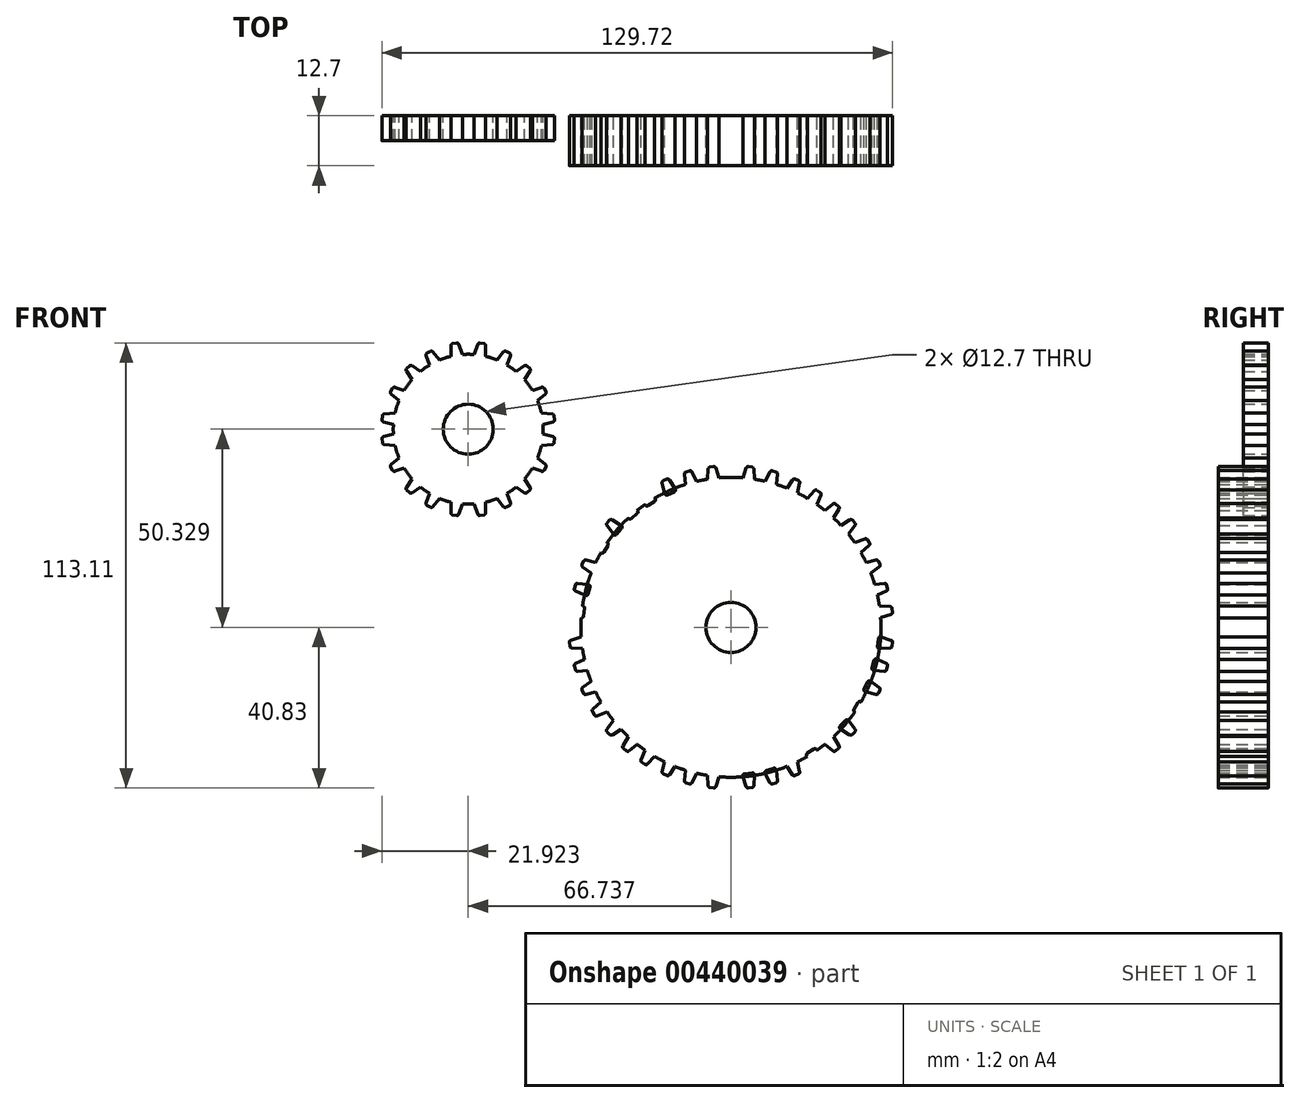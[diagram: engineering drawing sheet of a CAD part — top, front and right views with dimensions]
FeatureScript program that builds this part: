
annotation { "Feature Type Name" : "Feature", "Feature Type Description" : "" }
export const myFeature = defineFeature(function(context is Context, id is Id, definition is map)
    precondition{}
    {
        {
            var Q0;
            Q0=qCreatedBy(makeId("Front.planeOp"),FACE);
            var sketch = newSketch(context, id + "F0", { "sketchPlane" : qUnion([Q0])});
            skCircle(sketch, "E0", {"center": v(0, 0) * mm, "radius": 38.1 * mm});
            skCircle(sketch, "E1", {"center": v(0, 0) * mm, "radius": 6.35 * mm});
            skLineSegment(sketch, "E2", {"start": v(-38.1, 0) * mm, "end": v(38.1, 0) * mm, "construction": true});
            skLineSegment(sketch, "E3", {"start": v(0, 38.1) * mm, "end": v(0, -38.1) * mm, "construction": true});
            skLineSegment(sketch, "E4", {"start": v(35.83, 10.3) * mm, "end": v(36.32, 8.42) * mm});
            skLineSegment(sketch, "E5", {"start": v(39.02, 11.15) * mm, "end": v(36.28, 10.93) * mm});
            skLineSegment(sketch, "E6", {"start": v(37.02, 8.09) * mm, "end": v(39.52, 9.23) * mm});
            skLineSegment(sketch, "E7", {"start": v(39.55, 10.77) * mm, "end": v(39.8, 9.82) * mm});
            skPoint(sketch, "E8.visualSharp", {"position": v(39.44, 11.18) * mm});
            skArc(sketch, "E8.filletArc", {"start": v(39.55, 10.77) * mm, "mid": v(39.35, 11.06) * mm, "end": v(39.02, 11.15) * mm});
            skPoint(sketch, "E9.visualSharp", {"position": v(35.68, 10.88) * mm});
            skArc(sketch, "E9.filletArc", {"start": v(36.28, 10.93) * mm, "mid": v(35.91, 10.72) * mm, "end": v(35.83, 10.3) * mm});
            skPoint(sketch, "E10.visualSharp", {"position": v(36.47, 7.84) * mm});
            skArc(sketch, "E10.filletArc", {"start": v(36.32, 8.42) * mm, "mid": v(36.6, 8.1) * mm, "end": v(37.02, 8.09) * mm});
            skPoint(sketch, "E11.visualSharp", {"position": v(39.9, 9.4) * mm});
            skArc(sketch, "E11.filletArc", {"start": v(39.52, 9.23) * mm, "mid": v(39.76, 9.47) * mm, "end": v(39.8, 9.82) * mm});
            skLineSegment(sketch, "E12", {"start": v(37.18, 4.8) * mm, "end": v(37.43, 2.88) * mm});
            skLineSegment(sketch, "E13", {"start": v(40.44, 5.27) * mm, "end": v(37.7, 5.38) * mm});
            skLineSegment(sketch, "E14", {"start": v(38.1, 2.46) * mm, "end": v(40.7, 3.3) * mm});
            skLineSegment(sketch, "E15", {"start": v(40.92, 4.83) * mm, "end": v(41.05, 3.85) * mm});
            skPoint(sketch, "E16.visualSharp", {"position": v(40.87, 5.25) * mm});
            skArc(sketch, "E16.filletArc", {"start": v(40.92, 4.83) * mm, "mid": v(40.76, 5.13) * mm, "end": v(40.44, 5.27) * mm});
            skPoint(sketch, "E17.visualSharp", {"position": v(37.1, 5.4) * mm});
            skArc(sketch, "E17.filletArc", {"start": v(37.7, 5.38) * mm, "mid": v(37.3, 5.21) * mm, "end": v(37.18, 4.8) * mm});
            skPoint(sketch, "E18.visualSharp", {"position": v(37.52, 2.28) * mm});
            skArc(sketch, "E18.filletArc", {"start": v(37.43, 2.88) * mm, "mid": v(37.67, 2.52) * mm, "end": v(38.1, 2.46) * mm});
            skPoint(sketch, "E19.visualSharp", {"position": v(41.11, 3.43) * mm});
            skArc(sketch, "E19.filletArc", {"start": v(40.7, 3.3) * mm, "mid": v(40.98, 3.5) * mm, "end": v(41.05, 3.85) * mm});
            skLineSegment(sketch, "E20.0", {"start": v(41.11, 3.43) * mm, "end": v(40.87, 5.25) * mm, "construction": true});
            skLineSegment(sketch, "E21.0", {"start": v(39.9, 9.4) * mm, "end": v(39.44, 11.18) * mm, "construction": true});
            skLineSegment(sketch, "E22", {"start": v(33.84, 15.67) * mm, "end": v(34.66, 13.92) * mm});
            skLineSegment(sketch, "E23", {"start": v(36.81, 17.09) * mm, "end": v(34.17, 16.38) * mm});
            skLineSegment(sketch, "E24", {"start": v(35.4, 13.71) * mm, "end": v(37.65, 15.29) * mm});
            skLineSegment(sketch, "E25", {"start": v(37.4, 16.81) * mm, "end": v(37.82, 15.92) * mm});
            skPoint(sketch, "E26.visualSharp", {"position": v(37.23, 17.2) * mm});
            skArc(sketch, "E26.filletArc", {"start": v(37.4, 16.81) * mm, "mid": v(37.16, 17.06) * mm, "end": v(36.81, 17.09) * mm});
            skPoint(sketch, "E27.visualSharp", {"position": v(33.58, 16.22) * mm});
            skArc(sketch, "E27.filletArc", {"start": v(34.17, 16.38) * mm, "mid": v(33.84, 16.1) * mm, "end": v(33.84, 15.67) * mm});
            skPoint(sketch, "E28.visualSharp", {"position": v(34.91, 13.37) * mm});
            skArc(sketch, "E28.filletArc", {"start": v(34.66, 13.92) * mm, "mid": v(34.99, 13.64) * mm, "end": v(35.4, 13.71) * mm});
            skPoint(sketch, "E29.visualSharp", {"position": v(38, 15.53) * mm});
            skArc(sketch, "E29.filletArc", {"start": v(37.65, 15.29) * mm, "mid": v(37.85, 15.57) * mm, "end": v(37.82, 15.92) * mm});
            skLineSegment(sketch, "E30.0", {"start": v(38, 15.53) * mm, "end": v(37.23, 17.2) * mm, "construction": true});
            skLineSegment(sketch, "E31", {"start": v(31.25, 20.8) * mm, "end": v(32.23, 19.13) * mm});
            skLineSegment(sketch, "E32", {"start": v(34.08, 22.48) * mm, "end": v(31.51, 21.53) * mm});
            skLineSegment(sketch, "E33", {"start": v(33, 19) * mm, "end": v(35.09, 20.77) * mm});
            skLineSegment(sketch, "E34", {"start": v(34.7, 22.26) * mm, "end": v(35.2, 21.41) * mm});
            skPoint(sketch, "E35.visualSharp", {"position": v(34.48, 22.63) * mm});
            skArc(sketch, "E35.filletArc", {"start": v(34.7, 22.26) * mm, "mid": v(34.43, 22.49) * mm, "end": v(34.08, 22.48) * mm});
            skPoint(sketch, "E36.visualSharp", {"position": v(30.94, 21.32) * mm});
            skArc(sketch, "E36.filletArc", {"start": v(31.51, 21.53) * mm, "mid": v(31.2, 21.23) * mm, "end": v(31.25, 20.8) * mm});
            skPoint(sketch, "E37.visualSharp", {"position": v(32.53, 18.6) * mm});
            skArc(sketch, "E37.filletArc", {"start": v(32.23, 19.13) * mm, "mid": v(32.58, 18.88) * mm, "end": v(33, 19) * mm});
            skPoint(sketch, "E38.visualSharp", {"position": v(35.41, 21.04) * mm});
            skArc(sketch, "E38.filletArc", {"start": v(35.09, 20.77) * mm, "mid": v(35.26, 21.07) * mm, "end": v(35.2, 21.41) * mm});
            skLineSegment(sketch, "E39.0", {"start": v(35.41, 21.04) * mm, "end": v(34.48, 22.63) * mm, "construction": true});
            skLineSegment(sketch, "E40", {"start": v(27.75, 25.07) * mm, "end": v(29.06, 23.64) * mm});
            skLineSegment(sketch, "E41", {"start": v(30.16, 27.32) * mm, "end": v(27.85, 25.84) * mm});
            skLineSegment(sketch, "E42", {"start": v(29.84, 23.68) * mm, "end": v(31.5, 25.86) * mm});
            skLineSegment(sketch, "E43", {"start": v(30.8, 27.24) * mm, "end": v(31.47, 26.51) * mm});
            skPoint(sketch, "E44.visualSharp", {"position": v(30.52, 27.55) * mm});
            skArc(sketch, "E44.filletArc", {"start": v(30.8, 27.24) * mm, "mid": v(30.5, 27.4) * mm, "end": v(30.16, 27.32) * mm});
            skPoint(sketch, "E45.visualSharp", {"position": v(27.34, 25.51) * mm});
            skArc(sketch, "E45.filletArc", {"start": v(27.85, 25.84) * mm, "mid": v(27.62, 25.48) * mm, "end": v(27.75, 25.07) * mm});
            skPoint(sketch, "E46.visualSharp", {"position": v(29.47, 23.2) * mm});
            skArc(sketch, "E46.filletArc", {"start": v(29.06, 23.64) * mm, "mid": v(29.46, 23.48) * mm, "end": v(29.84, 23.68) * mm});
            skPoint(sketch, "E47.visualSharp", {"position": v(31.76, 26.2) * mm});
            skArc(sketch, "E47.filletArc", {"start": v(31.5, 25.86) * mm, "mid": v(31.6, 26.19) * mm, "end": v(31.47, 26.51) * mm});
            skLineSegment(sketch, "E48.0", {"start": v(31.76, 26.2) * mm, "end": v(30.52, 27.55) * mm, "construction": true});
            skLineSegment(sketch, "E49", {"start": v(23.82, 28.87) * mm, "end": v(25.3, 27.61) * mm});
            skLineSegment(sketch, "E50", {"start": v(25.95, 31.4) * mm, "end": v(23.83, 29.65) * mm});
            skLineSegment(sketch, "E51", {"start": v(26.07, 27.74) * mm, "end": v(27.46, 30.1) * mm});
            skLineSegment(sketch, "E52", {"start": v(26.6, 31.39) * mm, "end": v(27.35, 30.75) * mm});
            skPoint(sketch, "E53.visualSharp", {"position": v(26.28, 31.66) * mm});
            skArc(sketch, "E53.filletArc", {"start": v(26.6, 31.39) * mm, "mid": v(26.27, 31.5) * mm, "end": v(25.95, 31.4) * mm});
            skPoint(sketch, "E54.visualSharp", {"position": v(23.36, 29.26) * mm});
            skArc(sketch, "E54.filletArc", {"start": v(23.83, 29.65) * mm, "mid": v(23.65, 29.26) * mm, "end": v(23.82, 28.87) * mm});
            skPoint(sketch, "E55.visualSharp", {"position": v(25.76, 27.22) * mm});
            skArc(sketch, "E55.filletArc", {"start": v(25.3, 27.61) * mm, "mid": v(25.71, 27.5) * mm, "end": v(26.07, 27.74) * mm});
            skPoint(sketch, "E56.visualSharp", {"position": v(27.67, 30.47) * mm});
            skArc(sketch, "E56.filletArc", {"start": v(27.46, 30.1) * mm, "mid": v(27.52, 30.44) * mm, "end": v(27.35, 30.75) * mm});
            skLineSegment(sketch, "E57", {"start": v(19.42, 31.95) * mm, "end": v(21.04, 30.9) * mm});
            skLineSegment(sketch, "E58", {"start": v(21.18, 34.74) * mm, "end": v(19.32, 32.72) * mm});
            skLineSegment(sketch, "E59", {"start": v(21.79, 31.13) * mm, "end": v(22.85, 33.66) * mm});
            skLineSegment(sketch, "E60", {"start": v(21.83, 34.82) * mm, "end": v(22.66, 34.28) * mm});
            skPoint(sketch, "E61.visualSharp", {"position": v(21.47, 35.05) * mm});
            skArc(sketch, "E61.filletArc", {"start": v(21.83, 34.82) * mm, "mid": v(21.5, 34.9) * mm, "end": v(21.18, 34.74) * mm});
            skPoint(sketch, "E62.visualSharp", {"position": v(18.9, 32.28) * mm});
            skArc(sketch, "E62.filletArc", {"start": v(19.32, 32.72) * mm, "mid": v(19.19, 32.32) * mm, "end": v(19.42, 31.95) * mm});
            skPoint(sketch, "E63.visualSharp", {"position": v(21.55, 30.57) * mm});
            skArc(sketch, "E63.filletArc", {"start": v(21.04, 30.9) * mm, "mid": v(21.47, 30.84) * mm, "end": v(21.79, 31.13) * mm});
            skPoint(sketch, "E64.visualSharp", {"position": v(23.02, 34.05) * mm});
            skArc(sketch, "E64.filletArc", {"start": v(22.85, 33.66) * mm, "mid": v(22.87, 34) * mm, "end": v(22.66, 34.28) * mm});
            skLineSegment(sketch, "E65.0", {"start": v(23.02, 34.05) * mm, "end": v(21.47, 35.05) * mm, "construction": true});
            skLineSegment(sketch, "E66", {"start": v(14.37, 34.42) * mm, "end": v(16.15, 33.66) * mm});
            skLineSegment(sketch, "E67", {"start": v(15.63, 37.46) * mm, "end": v(14.14, 35.16) * mm});
            skLineSegment(sketch, "E68", {"start": v(16.85, 34.02) * mm, "end": v(17.46, 36.69) * mm});
            skLineSegment(sketch, "E69", {"start": v(16.26, 37.65) * mm, "end": v(17.17, 37.27) * mm});
            skPoint(sketch, "E70.visualSharp", {"position": v(15.87, 37.82) * mm});
            skArc(sketch, "E70.filletArc", {"start": v(16.26, 37.65) * mm, "mid": v(15.91, 37.67) * mm, "end": v(15.63, 37.46) * mm});
            skPoint(sketch, "E71.visualSharp", {"position": v(13.81, 34.66) * mm});
            skArc(sketch, "E71.filletArc", {"start": v(14.14, 35.16) * mm, "mid": v(14.08, 34.74) * mm, "end": v(14.37, 34.42) * mm});
            skPoint(sketch, "E72.visualSharp", {"position": v(16.71, 33.43) * mm});
            skArc(sketch, "E72.filletArc", {"start": v(16.15, 33.66) * mm, "mid": v(16.58, 33.68) * mm, "end": v(16.85, 34.02) * mm});
            skPoint(sketch, "E73.visualSharp", {"position": v(17.56, 37.1) * mm});
            skArc(sketch, "E73.filletArc", {"start": v(17.46, 36.69) * mm, "mid": v(17.42, 37.03) * mm, "end": v(17.17, 37.27) * mm});
            skLineSegment(sketch, "E74.0", {"start": v(17.56, 37.1) * mm, "end": v(15.87, 37.82) * mm, "construction": true});
            skLineSegment(sketch, "E75", {"start": v(9, 36.36) * mm, "end": v(10.84, 35.79) * mm});
            skLineSegment(sketch, "E76", {"start": v(9.94, 39.51) * mm, "end": v(8.69, 37.07) * mm});
            skLineSegment(sketch, "E77", {"start": v(11.5, 36.2) * mm, "end": v(11.84, 38.93) * mm});
            skLineSegment(sketch, "E78", {"start": v(10.54, 39.77) * mm, "end": v(11.48, 39.48) * mm});
            skPoint(sketch, "E79.visualSharp", {"position": v(10.13, 39.9) * mm});
            skArc(sketch, "E79.filletArc", {"start": v(10.54, 39.77) * mm, "mid": v(10.2, 39.75) * mm, "end": v(9.94, 39.51) * mm});
            skPoint(sketch, "E80.visualSharp", {"position": v(8.41, 36.53) * mm});
            skArc(sketch, "E80.filletArc", {"start": v(8.69, 37.07) * mm, "mid": v(8.67, 36.64) * mm, "end": v(9, 36.36) * mm});
            skPoint(sketch, "E81.visualSharp", {"position": v(11.42, 35.6) * mm});
            skArc(sketch, "E81.filletArc", {"start": v(10.84, 35.79) * mm, "mid": v(11.27, 35.85) * mm, "end": v(11.5, 36.2) * mm});
            skPoint(sketch, "E82.visualSharp", {"position": v(11.89, 39.35) * mm});
            skArc(sketch, "E82.filletArc", {"start": v(11.84, 38.93) * mm, "mid": v(11.76, 39.27) * mm, "end": v(11.48, 39.48) * mm});
            skLineSegment(sketch, "E83.0", {"start": v(11.89, 39.35) * mm, "end": v(10.13, 39.9) * mm, "construction": true});
            skLineSegment(sketch, "E84", {"start": v(3.43, 37.2) * mm, "end": v(5.36, 36.95) * mm});
            skLineSegment(sketch, "E85", {"start": v(3.84, 40.48) * mm, "end": v(3.01, 37.86) * mm});
            skLineSegment(sketch, "E86", {"start": v(5.93, 37.48) * mm, "end": v(5.8, 40.22) * mm});
            skLineSegment(sketch, "E87", {"start": v(4.39, 40.83) * mm, "end": v(5.36, 40.7) * mm});
            skPoint(sketch, "E88.visualSharp", {"position": v(3.96, 40.88) * mm});
            skArc(sketch, "E88.filletArc", {"start": v(4.39, 40.83) * mm, "mid": v(4.05, 40.75) * mm, "end": v(3.84, 40.48) * mm});
            skPoint(sketch, "E89.visualSharp", {"position": v(2.83, 37.28) * mm});
            skArc(sketch, "E89.filletArc", {"start": v(3.01, 37.86) * mm, "mid": v(3.07, 37.43) * mm, "end": v(3.43, 37.2) * mm});
            skPoint(sketch, "E90.visualSharp", {"position": v(5.96, 36.88) * mm});
            skArc(sketch, "E90.filletArc", {"start": v(5.36, 36.95) * mm, "mid": v(5.77, 37.08) * mm, "end": v(5.93, 37.48) * mm});
            skPoint(sketch, "E91.visualSharp", {"position": v(5.79, 40.65) * mm});
            skArc(sketch, "E91.filletArc", {"start": v(5.8, 40.22) * mm, "mid": v(5.67, 40.54) * mm, "end": v(5.36, 40.7) * mm});
            skLineSegment(sketch, "E92.0", {"start": v(5.79, 40.65) * mm, "end": v(3.96, 40.88) * mm, "construction": true});
            skLineSegment(sketch, "E93.MirrorCS", {"start": v(-16.26, 37.65) * mm, "end": v(-17.17, 37.27) * mm});
            skLineSegment(sketch, "E94.MirrorCS", {"start": v(-4.39, 40.83) * mm, "end": v(-5.36, 40.7) * mm});
            skLineSegment(sketch, "E95.MirrorCS", {"start": v(-39.55, 10.77) * mm, "end": v(-39.8, 9.82) * mm});
            skLineSegment(sketch, "E96.MirrorCS", {"start": v(-37.4, 16.81) * mm, "end": v(-37.82, 15.92) * mm});
            skArc(sketch, "E97.MirrorCS", {"start": v(-21.83, 34.82) * mm, "mid": v(-21.5, 34.9) * mm, "end": v(-21.18, 34.74) * mm});
            skArc(sketch, "E98.MirrorCS", {"start": v(-34.7, 22.26) * mm, "mid": v(-34.43, 22.49) * mm, "end": v(-34.08, 22.48) * mm});
            skArc(sketch, "E99.MirrorCS", {"start": v(-22.85, 33.66) * mm, "mid": v(-22.87, 34) * mm, "end": v(-22.66, 34.28) * mm});
            skArc(sketch, "E100.MirrorCS", {"start": v(-37.7, 5.38) * mm, "mid": v(-37.3, 5.21) * mm, "end": v(-37.18, 4.8) * mm});
            skLineSegment(sketch, "E101.MirrorCS", {"start": v(-21.83, 34.82) * mm, "end": v(-22.66, 34.28) * mm});
            skArc(sketch, "E102.MirrorCS", {"start": v(-39.52, 9.23) * mm, "mid": v(-39.76, 9.47) * mm, "end": v(-39.8, 9.82) * mm});
            skLineSegment(sketch, "E103.MirrorCS", {"start": v(-10.54, 39.77) * mm, "end": v(-11.48, 39.48) * mm});
            skLineSegment(sketch, "E104.MirrorCS", {"start": v(-30.8, 27.24) * mm, "end": v(-31.47, 26.51) * mm});
            skArc(sketch, "E105.MirrorCS", {"start": v(-17.46, 36.69) * mm, "mid": v(-17.42, 37.03) * mm, "end": v(-17.17, 37.27) * mm});
            skArc(sketch, "E106.MirrorCS", {"start": v(-31.51, 21.53) * mm, "mid": v(-31.2, 21.23) * mm, "end": v(-31.25, 20.8) * mm});
            skLineSegment(sketch, "E107.MirrorCS", {"start": v(-23.02, 34.05) * mm, "end": v(-21.47, 35.05) * mm, "construction": true});
            skArc(sketch, "E108.MirrorCS", {"start": v(-36.28, 10.93) * mm, "mid": v(-35.91, 10.72) * mm, "end": v(-35.83, 10.3) * mm});
            skArc(sketch, "E109.MirrorCS", {"start": v(-40.7, 3.3) * mm, "mid": v(-40.98, 3.5) * mm, "end": v(-41.05, 3.85) * mm});
            skArc(sketch, "E110.MirrorCS", {"start": v(-32.23, 19.13) * mm, "mid": v(-32.58, 18.88) * mm, "end": v(-33, 19) * mm});
            skArc(sketch, "E111.MirrorCS", {"start": v(-26.6, 31.39) * mm, "mid": v(-26.27, 31.5) * mm, "end": v(-25.95, 31.4) * mm});
            skLineSegment(sketch, "E112.MirrorCS", {"start": v(-3.84, 40.48) * mm, "end": v(-3.01, 37.86) * mm});
            skLineSegment(sketch, "E113.MirrorCS", {"start": v(-39.9, 9.4) * mm, "end": v(-39.44, 11.18) * mm, "construction": true});
            skArc(sketch, "E114.MirrorCS", {"start": v(-10.54, 39.77) * mm, "mid": v(-10.2, 39.75) * mm, "end": v(-9.94, 39.51) * mm});
            skArc(sketch, "E115.MirrorCS", {"start": v(-21.04, 30.9) * mm, "mid": v(-21.47, 30.84) * mm, "end": v(-21.79, 31.13) * mm});
            skArc(sketch, "E116.MirrorCS", {"start": v(-31.5, 25.86) * mm, "mid": v(-31.6, 26.19) * mm, "end": v(-31.47, 26.51) * mm});
            skLineSegment(sketch, "E117.MirrorCS", {"start": v(-31.25, 20.8) * mm, "end": v(-32.23, 19.13) * mm});
            skLineSegment(sketch, "E118.MirrorCS", {"start": v(-40.44, 5.27) * mm, "end": v(-37.7, 5.38) * mm});
            skLineSegment(sketch, "E119.MirrorCS", {"start": v(-38.1, 2.46) * mm, "end": v(-40.7, 3.3) * mm});
            skLineSegment(sketch, "E120.MirrorCS", {"start": v(-40.92, 4.83) * mm, "end": v(-41.05, 3.85) * mm});
            skLineSegment(sketch, "E121.MirrorCS", {"start": v(-33.84, 15.67) * mm, "end": v(-34.66, 13.92) * mm});
            skLineSegment(sketch, "E122.MirrorCS", {"start": v(-5.93, 37.48) * mm, "end": v(-5.8, 40.22) * mm});
            skArc(sketch, "E123.MirrorCS", {"start": v(-16.26, 37.65) * mm, "mid": v(-15.91, 37.67) * mm, "end": v(-15.63, 37.46) * mm});
            skArc(sketch, "E124.MirrorCS", {"start": v(-23.83, 29.65) * mm, "mid": v(-23.65, 29.26) * mm, "end": v(-23.82, 28.87) * mm});
            skArc(sketch, "E125.MirrorCS", {"start": v(-35.09, 20.77) * mm, "mid": v(-35.26, 21.07) * mm, "end": v(-35.2, 21.41) * mm});
            skLineSegment(sketch, "E126.MirrorCS", {"start": v(-35.83, 10.3) * mm, "end": v(-36.32, 8.42) * mm});
            skArc(sketch, "E127.MirrorCS", {"start": v(-25.3, 27.61) * mm, "mid": v(-25.71, 27.5) * mm, "end": v(-26.07, 27.74) * mm});
            skLineSegment(sketch, "E128.MirrorCS", {"start": v(-35.41, 21.04) * mm, "end": v(-34.48, 22.63) * mm, "construction": true});
            skLineSegment(sketch, "E129.MirrorCS", {"start": v(-36.81, 17.09) * mm, "end": v(-34.17, 16.38) * mm});
            skLineSegment(sketch, "E130.MirrorCS", {"start": v(-39.02, 11.15) * mm, "end": v(-36.28, 10.93) * mm});
            skLineSegment(sketch, "E131.MirrorCS", {"start": v(-41.11, 3.43) * mm, "end": v(-40.87, 5.25) * mm, "construction": true});
            skLineSegment(sketch, "E132.MirrorCS", {"start": v(-3.43, 37.2) * mm, "end": v(-5.36, 36.95) * mm});
            skLineSegment(sketch, "E133.MirrorCS", {"start": v(-37.02, 8.09) * mm, "end": v(-39.52, 9.23) * mm});
            skArc(sketch, "E134.MirrorCS", {"start": v(-14.14, 35.16) * mm, "mid": v(-14.08, 34.74) * mm, "end": v(-14.37, 34.42) * mm});
            skLineSegment(sketch, "E135.MirrorCS", {"start": v(-14.37, 34.42) * mm, "end": v(-16.15, 33.66) * mm});
            skArc(sketch, "E136.MirrorCS", {"start": v(-39.55, 10.77) * mm, "mid": v(-39.35, 11.06) * mm, "end": v(-39.02, 11.15) * mm});
            skArc(sketch, "E137.MirrorCS", {"start": v(-27.85, 25.84) * mm, "mid": v(-27.62, 25.48) * mm, "end": v(-27.75, 25.07) * mm});
            skLineSegment(sketch, "E138.MirrorCS", {"start": v(-30.16, 27.32) * mm, "end": v(-27.85, 25.84) * mm});
            skLineSegment(sketch, "E139.MirrorCS", {"start": v(-9, 36.36) * mm, "end": v(-10.84, 35.79) * mm});
            skLineSegment(sketch, "E140.MirrorCS", {"start": v(-21.79, 31.13) * mm, "end": v(-22.85, 33.66) * mm});
            skLineSegment(sketch, "E141.MirrorCS", {"start": v(-11.5, 36.2) * mm, "end": v(-11.84, 38.93) * mm});
            skArc(sketch, "E142.MirrorCS", {"start": v(-5.36, 36.95) * mm, "mid": v(-5.77, 37.08) * mm, "end": v(-5.93, 37.48) * mm});
            skLineSegment(sketch, "E143.MirrorCS", {"start": v(-34.7, 22.26) * mm, "end": v(-35.2, 21.41) * mm});
            skArc(sketch, "E144.MirrorCS", {"start": v(-11.84, 38.93) * mm, "mid": v(-11.76, 39.27) * mm, "end": v(-11.48, 39.48) * mm});
            skLineSegment(sketch, "E145.MirrorCS", {"start": v(-31.76, 26.2) * mm, "end": v(-30.52, 27.55) * mm, "construction": true});
            skLineSegment(sketch, "E146.MirrorCS", {"start": v(-34.08, 22.48) * mm, "end": v(-31.51, 21.53) * mm});
            skArc(sketch, "E147.MirrorCS", {"start": v(-3.01, 37.86) * mm, "mid": v(-3.07, 37.43) * mm, "end": v(-3.43, 37.2) * mm});
            skArc(sketch, "E148.MirrorCS", {"start": v(-10.84, 35.79) * mm, "mid": v(-11.27, 35.85) * mm, "end": v(-11.5, 36.2) * mm});
            skLineSegment(sketch, "E149.MirrorCS", {"start": v(-17.56, 37.1) * mm, "end": v(-15.87, 37.82) * mm, "construction": true});
            skLineSegment(sketch, "E150.MirrorCS", {"start": v(-26.07, 27.74) * mm, "end": v(-27.46, 30.1) * mm});
            skArc(sketch, "E151.MirrorCS", {"start": v(-34.17, 16.38) * mm, "mid": v(-33.84, 16.1) * mm, "end": v(-33.84, 15.67) * mm});
            skArc(sketch, "E152.MirrorCS", {"start": v(-37.65, 15.29) * mm, "mid": v(-37.85, 15.57) * mm, "end": v(-37.82, 15.92) * mm});
            skArc(sketch, "E153.MirrorCS", {"start": v(-37.4, 16.81) * mm, "mid": v(-37.16, 17.06) * mm, "end": v(-36.81, 17.09) * mm});
            skLineSegment(sketch, "E154.MirrorCS", {"start": v(-29.84, 23.68) * mm, "end": v(-31.5, 25.86) * mm});
            skLineSegment(sketch, "E155.MirrorCS", {"start": v(-21.18, 34.74) * mm, "end": v(-19.32, 32.72) * mm});
            skArc(sketch, "E156.MirrorCS", {"start": v(-30.8, 27.24) * mm, "mid": v(-30.5, 27.4) * mm, "end": v(-30.16, 27.32) * mm});
            skLineSegment(sketch, "E157.MirrorCS", {"start": v(-15.63, 37.46) * mm, "end": v(-14.14, 35.16) * mm});
            skLineSegment(sketch, "E158.MirrorCS", {"start": v(-5.79, 40.65) * mm, "end": v(-3.96, 40.88) * mm, "construction": true});
            skLineSegment(sketch, "E159.MirrorCS", {"start": v(-33, 19) * mm, "end": v(-35.09, 20.77) * mm});
            skLineSegment(sketch, "E160.MirrorCS", {"start": v(-23.82, 28.87) * mm, "end": v(-25.3, 27.61) * mm});
            skArc(sketch, "E161.MirrorCS", {"start": v(-19.32, 32.72) * mm, "mid": v(-19.19, 32.32) * mm, "end": v(-19.42, 31.95) * mm});
            skLineSegment(sketch, "E162.MirrorCS", {"start": v(-38, 15.53) * mm, "end": v(-37.23, 17.2) * mm, "construction": true});
            skArc(sketch, "E163.MirrorCS", {"start": v(-8.69, 37.07) * mm, "mid": v(-8.67, 36.64) * mm, "end": v(-9, 36.36) * mm});
            skLineSegment(sketch, "E164.MirrorCS", {"start": v(-37.18, 4.8) * mm, "end": v(-37.43, 2.88) * mm});
            skLineSegment(sketch, "E165.MirrorCS", {"start": v(-26.6, 31.39) * mm, "end": v(-27.35, 30.75) * mm});
            skLineSegment(sketch, "E166.MirrorCS", {"start": v(-25.95, 31.4) * mm, "end": v(-23.83, 29.65) * mm});
            skLineSegment(sketch, "E167.MirrorCS", {"start": v(-16.85, 34.02) * mm, "end": v(-17.46, 36.69) * mm});
            skArc(sketch, "E168.MirrorCS", {"start": v(-34.66, 13.92) * mm, "mid": v(-34.99, 13.64) * mm, "end": v(-35.4, 13.71) * mm});
            skLineSegment(sketch, "E169.MirrorCS", {"start": v(-19.42, 31.95) * mm, "end": v(-21.04, 30.9) * mm});
            skArc(sketch, "E170.MirrorCS", {"start": v(-27.46, 30.1) * mm, "mid": v(-27.52, 30.44) * mm, "end": v(-27.35, 30.75) * mm});
            skLineSegment(sketch, "E171.MirrorCS", {"start": v(-35.4, 13.71) * mm, "end": v(-37.65, 15.29) * mm});
            skLineSegment(sketch, "E172.MirrorCS", {"start": v(-11.89, 39.35) * mm, "end": v(-10.13, 39.9) * mm, "construction": true});
            skArc(sketch, "E173.MirrorCS", {"start": v(-4.39, 40.83) * mm, "mid": v(-4.05, 40.75) * mm, "end": v(-3.84, 40.48) * mm});
            skArc(sketch, "E174.MirrorCS", {"start": v(-16.15, 33.66) * mm, "mid": v(-16.58, 33.68) * mm, "end": v(-16.85, 34.02) * mm});
            skArc(sketch, "E175.MirrorCS", {"start": v(-40.92, 4.83) * mm, "mid": v(-40.76, 5.13) * mm, "end": v(-40.44, 5.27) * mm});
            skArc(sketch, "E176.MirrorCS", {"start": v(-5.8, 40.22) * mm, "mid": v(-5.67, 40.54) * mm, "end": v(-5.36, 40.7) * mm});
            skArc(sketch, "E177.MirrorCS", {"start": v(-37.43, 2.88) * mm, "mid": v(-37.67, 2.52) * mm, "end": v(-38.1, 2.46) * mm});
            skLineSegment(sketch, "E178.MirrorCS", {"start": v(-27.75, 25.07) * mm, "end": v(-29.06, 23.64) * mm});
            skLineSegment(sketch, "E179.MirrorCS", {"start": v(-9.94, 39.51) * mm, "end": v(-8.69, 37.07) * mm});
            skArc(sketch, "E180.MirrorCS", {"start": v(-29.06, 23.64) * mm, "mid": v(-29.46, 23.48) * mm, "end": v(-29.84, 23.68) * mm});
            skArc(sketch, "E181.MirrorCS", {"start": v(-36.32, 8.42) * mm, "mid": v(-36.6, 8.1) * mm, "end": v(-37.02, 8.09) * mm});
            skPoint(sketch, "E182.MirrorP", {"position": v(-30.94, 21.32) * mm});
            skPoint(sketch, "E183.MirrorP", {"position": v(-41.11, 3.43) * mm});
            skPoint(sketch, "E184.MirrorP", {"position": v(-5.79, 40.65) * mm});
            skPoint(sketch, "E185.MirrorP", {"position": v(-17.56, 37.1) * mm});
            skPoint(sketch, "E186.MirrorP", {"position": v(-27.67, 30.47) * mm});
            skPoint(sketch, "E187.MirrorP", {"position": v(-25.76, 27.22) * mm});
            skPoint(sketch, "E188.MirrorP", {"position": v(-32.53, 18.6) * mm});
            skPoint(sketch, "E189.MirrorP", {"position": v(-35.41, 21.04) * mm});
            skPoint(sketch, "E190.MirrorP", {"position": v(-21.47, 35.05) * mm});
            skPoint(sketch, "E191.MirrorP", {"position": v(-30.52, 27.55) * mm});
            skPoint(sketch, "E192.MirrorP", {"position": v(-37.23, 17.2) * mm});
            skPoint(sketch, "E193.MirrorP", {"position": v(-39.44, 11.18) * mm});
            skPoint(sketch, "E194.MirrorP", {"position": v(-10.13, 39.9) * mm});
            skPoint(sketch, "E195.MirrorP", {"position": v(-40.87, 5.25) * mm});
            skPoint(sketch, "E196.MirrorP", {"position": v(-23.36, 29.26) * mm});
            skPoint(sketch, "E197.MirrorP", {"position": v(-33.58, 16.22) * mm});
            skPoint(sketch, "E198.MirrorP", {"position": v(-35.68, 10.88) * mm});
            skPoint(sketch, "E199.MirrorP", {"position": v(-18.9, 32.28) * mm});
            skPoint(sketch, "E200.MirrorP", {"position": v(-34.48, 22.63) * mm});
            skPoint(sketch, "E201.MirrorP", {"position": v(-15.87, 37.82) * mm});
            skPoint(sketch, "E202.MirrorP", {"position": v(-3.96, 40.88) * mm});
            skPoint(sketch, "E203.MirrorP", {"position": v(-8.41, 36.53) * mm});
            skPoint(sketch, "E204.MirrorP", {"position": v(-26.28, 31.66) * mm});
            skPoint(sketch, "E205.MirrorP", {"position": v(-27.34, 25.51) * mm});
            skPoint(sketch, "E206.MirrorP", {"position": v(-39.9, 9.4) * mm});
            skPoint(sketch, "E207.MirrorP", {"position": v(-23.02, 34.05) * mm});
            skPoint(sketch, "E208.MirrorP", {"position": v(-37.52, 2.28) * mm});
            skPoint(sketch, "E209.MirrorP", {"position": v(-21.55, 30.57) * mm});
            skPoint(sketch, "E210.MirrorP", {"position": v(-29.47, 23.2) * mm});
            skPoint(sketch, "E211.MirrorP", {"position": v(-34.91, 13.37) * mm});
            skPoint(sketch, "E212.MirrorP", {"position": v(-2.83, 37.28) * mm});
            skPoint(sketch, "E213.MirrorP", {"position": v(-16.71, 33.43) * mm});
            skPoint(sketch, "E214.MirrorP", {"position": v(-37.1, 5.4) * mm});
            skPoint(sketch, "E215.MirrorP", {"position": v(-13.81, 34.66) * mm});
            skPoint(sketch, "E216.MirrorP", {"position": v(-5.96, 36.88) * mm});
            skPoint(sketch, "E217.MirrorP", {"position": v(-31.76, 26.2) * mm});
            skPoint(sketch, "E218.MirrorP", {"position": v(-11.89, 39.35) * mm});
            skPoint(sketch, "E219.MirrorP", {"position": v(-38, 15.53) * mm});
            skPoint(sketch, "E220.MirrorP", {"position": v(-36.47, 7.84) * mm});
            skPoint(sketch, "E221.MirrorP", {"position": v(-11.42, 35.6) * mm});
            skLineSegment(sketch, "E222.MirrorCS", {"start": v(40.92, -4.83) * mm, "end": v(41.05, -3.85) * mm});
            skLineSegment(sketch, "E223.MirrorCS", {"start": v(-4.39, -40.83) * mm, "end": v(-5.36, -40.7) * mm});
            skArc(sketch, "E224.MirrorCS", {"start": v(-4.39, -40.83) * mm, "mid": v(-4.05, -40.75) * mm, "end": v(-3.84, -40.48) * mm});
            skLineSegment(sketch, "E225.MirrorCS", {"start": v(16.26, -37.65) * mm, "end": v(17.17, -37.27) * mm});
            skArc(sketch, "E226.MirrorCS", {"start": v(-10.54, -39.77) * mm, "mid": v(-10.2, -39.75) * mm, "end": v(-9.94, -39.51) * mm});
            skLineSegment(sketch, "E227.MirrorCS", {"start": v(23.02, -34.05) * mm, "end": v(21.47, -35.05) * mm, "construction": true});
            skArc(sketch, "E228.MirrorCS", {"start": v(-37.43, -2.88) * mm, "mid": v(-37.67, -2.52) * mm, "end": v(-38.1, -2.46) * mm});
            skArc(sketch, "E229.MirrorCS", {"start": v(22.85, -33.66) * mm, "mid": v(22.87, -34) * mm, "end": v(22.66, -34.28) * mm});
            skArc(sketch, "E230.MirrorCS", {"start": v(40.92, -4.83) * mm, "mid": v(40.76, -5.13) * mm, "end": v(40.44, -5.27) * mm});
            skLineSegment(sketch, "E231.MirrorCS", {"start": v(-37.4, -16.81) * mm, "end": v(-37.82, -15.92) * mm});
            skArc(sketch, "E232.MirrorCS", {"start": v(36.28, -10.93) * mm, "mid": v(35.91, -10.72) * mm, "end": v(35.83, -10.3) * mm});
            skLineSegment(sketch, "E233.MirrorCS", {"start": v(39.55, -10.77) * mm, "end": v(39.8, -9.82) * mm});
            skArc(sketch, "E234.MirrorCS", {"start": v(-32.23, -19.13) * mm, "mid": v(-32.58, -18.88) * mm, "end": v(-33, -19) * mm});
            skLineSegment(sketch, "E235.MirrorCS", {"start": v(10.54, -39.77) * mm, "end": v(11.48, -39.48) * mm});
            skLineSegment(sketch, "E236.MirrorCS", {"start": v(21.83, -34.82) * mm, "end": v(22.66, -34.28) * mm});
            skArc(sketch, "E237.MirrorCS", {"start": v(-16.26, -37.65) * mm, "mid": v(-15.91, -37.67) * mm, "end": v(-15.63, -37.46) * mm});
            skArc(sketch, "E238.MirrorCS", {"start": v(-35.09, -20.77) * mm, "mid": v(-35.26, -21.07) * mm, "end": v(-35.2, -21.41) * mm});
            skArc(sketch, "E239.MirrorCS", {"start": v(-37.4, -16.81) * mm, "mid": v(-37.16, -17.06) * mm, "end": v(-36.81, -17.09) * mm});
            skLineSegment(sketch, "E240.MirrorCS", {"start": v(30.8, -27.24) * mm, "end": v(31.47, -26.51) * mm});
            skArc(sketch, "E241.MirrorCS", {"start": v(17.46, -36.69) * mm, "mid": v(17.42, -37.03) * mm, "end": v(17.17, -37.27) * mm});
            skLineSegment(sketch, "E242.MirrorCS", {"start": v(37.4, -16.81) * mm, "end": v(37.82, -15.92) * mm});
            skArc(sketch, "E243.MirrorCS", {"start": v(37.4, -16.81) * mm, "mid": v(37.16, -17.06) * mm, "end": v(36.81, -17.09) * mm});
            skArc(sketch, "E244.MirrorCS", {"start": v(-22.85, -33.66) * mm, "mid": v(-22.87, -34) * mm, "end": v(-22.66, -34.28) * mm});
            skArc(sketch, "E245.MirrorCS", {"start": v(16.26, -37.65) * mm, "mid": v(15.91, -37.67) * mm, "end": v(15.63, -37.46) * mm});
            skLineSegment(sketch, "E246.MirrorCS", {"start": v(-10.54, -39.77) * mm, "end": v(-11.48, -39.48) * mm});
            skArc(sketch, "E247.MirrorCS", {"start": v(-34.17, -16.38) * mm, "mid": v(-33.84, -16.1) * mm, "end": v(-33.84, -15.67) * mm});
            skArc(sketch, "E248.MirrorCS", {"start": v(35.09, -20.77) * mm, "mid": v(35.26, -21.07) * mm, "end": v(35.2, -21.41) * mm});
            skLineSegment(sketch, "E249.MirrorCS", {"start": v(4.39, -40.83) * mm, "end": v(5.36, -40.7) * mm});
            skLineSegment(sketch, "E250.MirrorCS", {"start": v(17.56, -37.1) * mm, "end": v(15.87, -37.82) * mm, "construction": true});
            skArc(sketch, "E251.MirrorCS", {"start": v(4.39, -40.83) * mm, "mid": v(4.05, -40.75) * mm, "end": v(3.84, -40.48) * mm});
            skLineSegment(sketch, "E252.MirrorCS", {"start": v(-21.83, -34.82) * mm, "end": v(-22.66, -34.28) * mm});
            skArc(sketch, "E253.MirrorCS", {"start": v(40.7, -3.3) * mm, "mid": v(40.98, -3.5) * mm, "end": v(41.05, -3.85) * mm});
            skLineSegment(sketch, "E254.MirrorCS", {"start": v(-40.92, -4.83) * mm, "end": v(-41.05, -3.85) * mm});
            skArc(sketch, "E255.MirrorCS", {"start": v(32.23, -19.13) * mm, "mid": v(32.58, -18.88) * mm, "end": v(33, -19) * mm});
            skLineSegment(sketch, "E256.MirrorCS", {"start": v(-23.02, -34.05) * mm, "end": v(-21.47, -35.05) * mm, "construction": true});
            skLineSegment(sketch, "E257.MirrorCS", {"start": v(41.11, -3.43) * mm, "end": v(40.87, -5.25) * mm, "construction": true});
            skLineSegment(sketch, "E258.MirrorCS", {"start": v(-38, -15.53) * mm, "end": v(-37.23, -17.2) * mm, "construction": true});
            skLineSegment(sketch, "E259.MirrorCS", {"start": v(-27.75, -25.07) * mm, "end": v(-29.06, -23.64) * mm});
            skArc(sketch, "E260.MirrorCS", {"start": v(-34.7, -22.26) * mm, "mid": v(-34.43, -22.49) * mm, "end": v(-34.08, -22.48) * mm});
            skLineSegment(sketch, "E261.MirrorCS", {"start": v(-34.08, -22.48) * mm, "end": v(-31.51, -21.53) * mm});
            skLineSegment(sketch, "E262.MirrorCS", {"start": v(34.7, -22.26) * mm, "end": v(35.2, -21.41) * mm});
            skLineSegment(sketch, "E263.MirrorCS", {"start": v(25.95, -31.4) * mm, "end": v(23.83, -29.65) * mm});
            skLineSegment(sketch, "E264.MirrorCS", {"start": v(14.37, -34.42) * mm, "end": v(16.15, -33.66) * mm});
            skArc(sketch, "E265.MirrorCS", {"start": v(11.84, -38.93) * mm, "mid": v(11.76, -39.27) * mm, "end": v(11.48, -39.48) * mm});
            skArc(sketch, "E266.MirrorCS", {"start": v(37.43, -2.88) * mm, "mid": v(37.67, -2.52) * mm, "end": v(38.1, -2.46) * mm});
            skArc(sketch, "E267.MirrorCS", {"start": v(-21.83, -34.82) * mm, "mid": v(-21.5, -34.9) * mm, "end": v(-21.18, -34.74) * mm});
            skLineSegment(sketch, "E268.MirrorCS", {"start": v(-39.9, -9.4) * mm, "end": v(-39.44, -11.18) * mm, "construction": true});
            skLineSegment(sketch, "E269.MirrorCS", {"start": v(-36.81, -17.09) * mm, "end": v(-34.17, -16.38) * mm});
            skLineSegment(sketch, "E270.MirrorCS", {"start": v(-31.76, -26.2) * mm, "end": v(-30.52, -27.55) * mm, "construction": true});
            skLineSegment(sketch, "E271.MirrorCS", {"start": v(33, -19) * mm, "end": v(35.09, -20.77) * mm});
            skLineSegment(sketch, "E272.MirrorCS", {"start": v(23.82, -28.87) * mm, "end": v(25.3, -27.61) * mm});
            skArc(sketch, "E273.MirrorCS", {"start": v(10.84, -35.79) * mm, "mid": v(11.27, -35.85) * mm, "end": v(11.5, -36.2) * mm});
            skArc(sketch, "E274.MirrorCS", {"start": v(37.7, -5.38) * mm, "mid": v(37.3, -5.21) * mm, "end": v(37.18, -4.8) * mm});
            skArc(sketch, "E275.MirrorCS", {"start": v(-19.32, -32.72) * mm, "mid": v(-19.19, -32.32) * mm, "end": v(-19.42, -31.95) * mm});
            skLineSegment(sketch, "E276.MirrorCS", {"start": v(34.08, -22.48) * mm, "end": v(31.51, -21.53) * mm});
            skLineSegment(sketch, "E277.MirrorCS", {"start": v(31.76, -26.2) * mm, "end": v(30.52, -27.55) * mm, "construction": true});
            skArc(sketch, "E278.MirrorCS", {"start": v(8.69, -37.07) * mm, "mid": v(8.67, -36.64) * mm, "end": v(9, -36.36) * mm});
            skLineSegment(sketch, "E279.MirrorCS", {"start": v(-23.82, -28.87) * mm, "end": v(-25.3, -27.61) * mm});
            skArc(sketch, "E280.MirrorCS", {"start": v(-5.8, -40.22) * mm, "mid": v(-5.67, -40.54) * mm, "end": v(-5.36, -40.7) * mm});
            skLineSegment(sketch, "E281.MirrorCS", {"start": v(-35.41, -21.04) * mm, "end": v(-34.48, -22.63) * mm, "construction": true});
            skArc(sketch, "E282.MirrorCS", {"start": v(-11.84, -38.93) * mm, "mid": v(-11.76, -39.27) * mm, "end": v(-11.48, -39.48) * mm});
            skLineSegment(sketch, "E283.MirrorCS", {"start": v(37.18, -4.8) * mm, "end": v(37.43, -2.88) * mm});
            skArc(sketch, "E284.MirrorCS", {"start": v(39.52, -9.23) * mm, "mid": v(39.76, -9.47) * mm, "end": v(39.8, -9.82) * mm});
            skArc(sketch, "E285.MirrorCS", {"start": v(36.32, -8.42) * mm, "mid": v(36.6, -8.1) * mm, "end": v(37.02, -8.09) * mm});
            skArc(sketch, "E286.MirrorCS", {"start": v(39.55, -10.77) * mm, "mid": v(39.35, -11.06) * mm, "end": v(39.02, -11.15) * mm});
            skLineSegment(sketch, "E287.MirrorCS", {"start": v(37.02, -8.09) * mm, "end": v(39.52, -9.23) * mm});
            skLineSegment(sketch, "E288.MirrorCS", {"start": v(39.02, -11.15) * mm, "end": v(36.28, -10.93) * mm});
            skLineSegment(sketch, "E289.MirrorCS", {"start": v(35.83, -10.3) * mm, "end": v(36.32, -8.42) * mm});
            skLineSegment(sketch, "E290.MirrorCS", {"start": v(38.1, -2.46) * mm, "end": v(40.7, -3.3) * mm});
            skLineSegment(sketch, "E291.MirrorCS", {"start": v(40.44, -5.27) * mm, "end": v(37.7, -5.38) * mm});
            skLineSegment(sketch, "E292.MirrorCS", {"start": v(-33, -19) * mm, "end": v(-35.09, -20.77) * mm});
            skArc(sketch, "E293.MirrorCS", {"start": v(-40.92, -4.83) * mm, "mid": v(-40.76, -5.13) * mm, "end": v(-40.44, -5.27) * mm});
            skLineSegment(sketch, "E294.MirrorCS", {"start": v(-39.55, -10.77) * mm, "end": v(-39.8, -9.82) * mm});
            skArc(sketch, "E295.MirrorCS", {"start": v(-26.6, -31.39) * mm, "mid": v(-26.27, -31.5) * mm, "end": v(-25.95, -31.4) * mm});
            skArc(sketch, "E296.MirrorCS", {"start": v(-25.3, -27.61) * mm, "mid": v(-25.71, -27.5) * mm, "end": v(-26.07, -27.74) * mm});
            skLineSegment(sketch, "E297.MirrorCS", {"start": v(-34.7, -22.26) * mm, "end": v(-35.2, -21.41) * mm});
            skLineSegment(sketch, "E298.MirrorCS", {"start": v(31.25, -20.8) * mm, "end": v(32.23, -19.13) * mm});
            skArc(sketch, "E299.MirrorCS", {"start": v(31.5, -25.86) * mm, "mid": v(31.6, -26.19) * mm, "end": v(31.47, -26.51) * mm});
            skArc(sketch, "E300.MirrorCS", {"start": v(21.04, -30.9) * mm, "mid": v(21.47, -30.84) * mm, "end": v(21.79, -31.13) * mm});
            skArc(sketch, "E301.MirrorCS", {"start": v(10.54, -39.77) * mm, "mid": v(10.2, -39.75) * mm, "end": v(9.94, -39.51) * mm});
            skLineSegment(sketch, "E302.MirrorCS", {"start": v(-5.79, -40.65) * mm, "end": v(-3.96, -40.88) * mm, "construction": true});
            skArc(sketch, "E303.MirrorCS", {"start": v(-16.15, -33.66) * mm, "mid": v(-16.58, -33.68) * mm, "end": v(-16.85, -34.02) * mm});
            skLineSegment(sketch, "E304.MirrorCS", {"start": v(-35.83, -10.3) * mm, "end": v(-36.32, -8.42) * mm});
            skArc(sketch, "E305.MirrorCS", {"start": v(-5.36, -36.95) * mm, "mid": v(-5.77, -37.08) * mm, "end": v(-5.93, -37.48) * mm});
            skLineSegment(sketch, "E306.MirrorCS", {"start": v(38, -15.53) * mm, "end": v(37.23, -17.2) * mm, "construction": true});
            skArc(sketch, "E307.MirrorCS", {"start": v(29.06, -23.64) * mm, "mid": v(29.46, -23.48) * mm, "end": v(29.84, -23.68) * mm});
            skArc(sketch, "E308.MirrorCS", {"start": v(19.32, -32.72) * mm, "mid": v(19.19, -32.32) * mm, "end": v(19.42, -31.95) * mm});
            skLineSegment(sketch, "E309.MirrorCS", {"start": v(-21.79, -31.13) * mm, "end": v(-22.85, -33.66) * mm});
            skArc(sketch, "E310.MirrorCS", {"start": v(-30.8, -27.24) * mm, "mid": v(-30.5, -27.4) * mm, "end": v(-30.16, -27.32) * mm});
            skLineSegment(sketch, "E311.MirrorCS", {"start": v(-11.89, -39.35) * mm, "end": v(-10.13, -39.9) * mm, "construction": true});
            skLineSegment(sketch, "E312.MirrorCS", {"start": v(9.94, -39.51) * mm, "end": v(8.69, -37.07) * mm});
            skLineSegment(sketch, "E313.MirrorCS", {"start": v(5.79, -40.65) * mm, "end": v(3.96, -40.88) * mm, "construction": true});
            skArc(sketch, "E314.MirrorCS", {"start": v(-36.28, -10.93) * mm, "mid": v(-35.91, -10.72) * mm, "end": v(-35.83, -10.3) * mm});
            skArc(sketch, "E315.MirrorCS", {"start": v(-23.83, -29.65) * mm, "mid": v(-23.65, -29.26) * mm, "end": v(-23.82, -28.87) * mm});
            skArc(sketch, "E316.MirrorCS", {"start": v(34.66, -13.92) * mm, "mid": v(34.99, -13.64) * mm, "end": v(35.4, -13.71) * mm});
            skArc(sketch, "E317.MirrorCS", {"start": v(30.8, -27.24) * mm, "mid": v(30.5, -27.4) * mm, "end": v(30.16, -27.32) * mm});
            skLineSegment(sketch, "E318.MirrorCS", {"start": v(-15.63, -37.46) * mm, "end": v(-14.14, -35.16) * mm});
            skLineSegment(sketch, "E319.MirrorCS", {"start": v(-16.26, -37.65) * mm, "end": v(-17.17, -37.27) * mm});
            skLineSegment(sketch, "E320.MirrorCS", {"start": v(21.18, -34.74) * mm, "end": v(19.32, -32.72) * mm});
            skArc(sketch, "E321.MirrorCS", {"start": v(-40.7, -3.3) * mm, "mid": v(-40.98, -3.5) * mm, "end": v(-41.05, -3.85) * mm});
            skArc(sketch, "E322.MirrorCS", {"start": v(37.65, -15.29) * mm, "mid": v(37.85, -15.57) * mm, "end": v(37.82, -15.92) * mm});
            skArc(sketch, "E323.MirrorCS", {"start": v(27.85, -25.84) * mm, "mid": v(27.62, -25.48) * mm, "end": v(27.75, -25.07) * mm});
            skArc(sketch, "E324.MirrorCS", {"start": v(21.83, -34.82) * mm, "mid": v(21.5, -34.9) * mm, "end": v(21.18, -34.74) * mm});
            skLineSegment(sketch, "E325.MirrorCS", {"start": v(11.5, -36.2) * mm, "end": v(11.84, -38.93) * mm});
            skLineSegment(sketch, "E326.MirrorCS", {"start": v(29.84, -23.68) * mm, "end": v(31.5, -25.86) * mm});
            skLineSegment(sketch, "E327.MirrorCS", {"start": v(3.84, -40.48) * mm, "end": v(3.01, -37.86) * mm});
            skLineSegment(sketch, "E328.MirrorCS", {"start": v(39.9, -9.4) * mm, "end": v(39.44, -11.18) * mm, "construction": true});
            skArc(sketch, "E329.MirrorCS", {"start": v(34.17, -16.38) * mm, "mid": v(33.84, -16.1) * mm, "end": v(33.84, -15.67) * mm});
            skArc(sketch, "E330.MirrorCS", {"start": v(-27.85, -25.84) * mm, "mid": v(-27.62, -25.48) * mm, "end": v(-27.75, -25.07) * mm});
            skLineSegment(sketch, "E331.MirrorCS", {"start": v(-19.42, -31.95) * mm, "end": v(-21.04, -30.9) * mm});
            skArc(sketch, "E332.MirrorCS", {"start": v(3.01, -37.86) * mm, "mid": v(3.07, -37.43) * mm, "end": v(3.43, -37.2) * mm});
            skArc(sketch, "E333.MirrorCS", {"start": v(-17.46, -36.69) * mm, "mid": v(-17.42, -37.03) * mm, "end": v(-17.17, -37.27) * mm});
            skLineSegment(sketch, "E334.MirrorCS", {"start": v(21.79, -31.13) * mm, "end": v(22.85, -33.66) * mm});
            skLineSegment(sketch, "E335.MirrorCS", {"start": v(-33.84, -15.67) * mm, "end": v(-34.66, -13.92) * mm});
            skLineSegment(sketch, "E336.MirrorCS", {"start": v(30.16, -27.32) * mm, "end": v(27.85, -25.84) * mm});
            skLineSegment(sketch, "E337.MirrorCS", {"start": v(-9, -36.36) * mm, "end": v(-10.84, -35.79) * mm});
            skLineSegment(sketch, "E338.MirrorCS", {"start": v(-21.18, -34.74) * mm, "end": v(-19.32, -32.72) * mm});
            skLineSegment(sketch, "E339.MirrorCS", {"start": v(-37.18, -4.8) * mm, "end": v(-37.43, -2.88) * mm});
            skArc(sketch, "E340.MirrorCS", {"start": v(-29.06, -23.64) * mm, "mid": v(-29.46, -23.48) * mm, "end": v(-29.84, -23.68) * mm});
            skArc(sketch, "E341.MirrorCS", {"start": v(-37.7, -5.38) * mm, "mid": v(-37.3, -5.21) * mm, "end": v(-37.18, -4.8) * mm});
            skArc(sketch, "E342.MirrorCS", {"start": v(-31.5, -25.86) * mm, "mid": v(-31.6, -26.19) * mm, "end": v(-31.47, -26.51) * mm});
            skLineSegment(sketch, "E343.MirrorCS", {"start": v(19.42, -31.95) * mm, "end": v(21.04, -30.9) * mm});
            skLineSegment(sketch, "E344.MirrorCS", {"start": v(-3.43, -37.2) * mm, "end": v(-5.36, -36.95) * mm});
            skArc(sketch, "E345.MirrorCS", {"start": v(-10.84, -35.79) * mm, "mid": v(-11.27, -35.85) * mm, "end": v(-11.5, -36.2) * mm});
            skArc(sketch, "E346.MirrorCS", {"start": v(31.51, -21.53) * mm, "mid": v(31.2, -21.23) * mm, "end": v(31.25, -20.8) * mm});
            skLineSegment(sketch, "E347.MirrorCS", {"start": v(26.6, -31.39) * mm, "end": v(27.35, -30.75) * mm});
            skLineSegment(sketch, "E348.MirrorCS", {"start": v(-14.37, -34.42) * mm, "end": v(-16.15, -33.66) * mm});
            skLineSegment(sketch, "E349.MirrorCS", {"start": v(-30.8, -27.24) * mm, "end": v(-31.47, -26.51) * mm});
            skLineSegment(sketch, "E350.MirrorCS", {"start": v(-38.1, -2.46) * mm, "end": v(-40.7, -3.3) * mm});
            skArc(sketch, "E351.MirrorCS", {"start": v(-39.52, -9.23) * mm, "mid": v(-39.76, -9.47) * mm, "end": v(-39.8, -9.82) * mm});
            skArc(sketch, "E352.MirrorCS", {"start": v(14.14, -35.16) * mm, "mid": v(14.08, -34.74) * mm, "end": v(14.37, -34.42) * mm});
            skLineSegment(sketch, "E353.MirrorCS", {"start": v(-25.95, -31.4) * mm, "end": v(-23.83, -29.65) * mm});
            skLineSegment(sketch, "E354.MirrorCS", {"start": v(-41.11, -3.43) * mm, "end": v(-40.87, -5.25) * mm, "construction": true});
            skLineSegment(sketch, "E355.MirrorCS", {"start": v(35.41, -21.04) * mm, "end": v(34.48, -22.63) * mm, "construction": true});
            skArc(sketch, "E356.MirrorCS", {"start": v(-8.69, -37.07) * mm, "mid": v(-8.67, -36.64) * mm, "end": v(-9, -36.36) * mm});
            skLineSegment(sketch, "E357.MirrorCS", {"start": v(-9.94, -39.51) * mm, "end": v(-8.69, -37.07) * mm});
            skArc(sketch, "E358.MirrorCS", {"start": v(23.83, -29.65) * mm, "mid": v(23.65, -29.26) * mm, "end": v(23.82, -28.87) * mm});
            skLineSegment(sketch, "E359.MirrorCS", {"start": v(36.81, -17.09) * mm, "end": v(34.17, -16.38) * mm});
            skLineSegment(sketch, "E360.MirrorCS", {"start": v(-26.07, -27.74) * mm, "end": v(-27.46, -30.1) * mm});
            skLineSegment(sketch, "E361.MirrorCS", {"start": v(15.63, -37.46) * mm, "end": v(14.14, -35.16) * mm});
            skLineSegment(sketch, "E362.MirrorCS", {"start": v(-40.44, -5.27) * mm, "end": v(-37.7, -5.38) * mm});
            skLineSegment(sketch, "E363.MirrorCS", {"start": v(26.07, -27.74) * mm, "end": v(27.46, -30.1) * mm});
            skArc(sketch, "E364.MirrorCS", {"start": v(-14.14, -35.16) * mm, "mid": v(-14.08, -34.74) * mm, "end": v(-14.37, -34.42) * mm});
            skArc(sketch, "E365.MirrorCS", {"start": v(-21.04, -30.9) * mm, "mid": v(-21.47, -30.84) * mm, "end": v(-21.79, -31.13) * mm});
            skArc(sketch, "E366.MirrorCS", {"start": v(-27.46, -30.1) * mm, "mid": v(-27.52, -30.44) * mm, "end": v(-27.35, -30.75) * mm});
            skArc(sketch, "E367.MirrorCS", {"start": v(34.7, -22.26) * mm, "mid": v(34.43, -22.49) * mm, "end": v(34.08, -22.48) * mm});
            skArc(sketch, "E368.MirrorCS", {"start": v(25.3, -27.61) * mm, "mid": v(25.71, -27.5) * mm, "end": v(26.07, -27.74) * mm});
            skArc(sketch, "E369.MirrorCS", {"start": v(-3.01, -37.86) * mm, "mid": v(-3.07, -37.43) * mm, "end": v(-3.43, -37.2) * mm});
            skArc(sketch, "E370.MirrorCS", {"start": v(5.8, -40.22) * mm, "mid": v(5.67, -40.54) * mm, "end": v(5.36, -40.7) * mm});
            skArc(sketch, "E371.MirrorCS", {"start": v(5.36, -36.95) * mm, "mid": v(5.77, -37.08) * mm, "end": v(5.93, -37.48) * mm});
            skArc(sketch, "E372.MirrorCS", {"start": v(26.6, -31.39) * mm, "mid": v(26.27, -31.5) * mm, "end": v(25.95, -31.4) * mm});
            skArc(sketch, "E373.MirrorCS", {"start": v(27.46, -30.1) * mm, "mid": v(27.52, -30.44) * mm, "end": v(27.35, -30.75) * mm});
            skLineSegment(sketch, "E374.MirrorCS", {"start": v(-29.84, -23.68) * mm, "end": v(-31.5, -25.86) * mm});
            skLineSegment(sketch, "E375.MirrorCS", {"start": v(11.89, -39.35) * mm, "end": v(10.13, -39.9) * mm, "construction": true});
            skArc(sketch, "E376.MirrorCS", {"start": v(-36.32, -8.42) * mm, "mid": v(-36.6, -8.1) * mm, "end": v(-37.02, -8.09) * mm});
            skArc(sketch, "E377.MirrorCS", {"start": v(-31.51, -21.53) * mm, "mid": v(-31.2, -21.23) * mm, "end": v(-31.25, -20.8) * mm});
            skArc(sketch, "E378.MirrorCS", {"start": v(-37.65, -15.29) * mm, "mid": v(-37.85, -15.57) * mm, "end": v(-37.82, -15.92) * mm});
            skArc(sketch, "E379.MirrorCS", {"start": v(-39.55, -10.77) * mm, "mid": v(-39.35, -11.06) * mm, "end": v(-39.02, -11.15) * mm});
            skLineSegment(sketch, "E380.MirrorCS", {"start": v(5.93, -37.48) * mm, "end": v(5.8, -40.22) * mm});
            skLineSegment(sketch, "E381.MirrorCS", {"start": v(9, -36.36) * mm, "end": v(10.84, -35.79) * mm});
            skLineSegment(sketch, "E382.MirrorCS", {"start": v(-17.56, -37.1) * mm, "end": v(-15.87, -37.82) * mm, "construction": true});
            skArc(sketch, "E383.MirrorCS", {"start": v(-34.66, -13.92) * mm, "mid": v(-34.99, -13.64) * mm, "end": v(-35.4, -13.71) * mm});
            skLineSegment(sketch, "E384.MirrorCS", {"start": v(35.4, -13.71) * mm, "end": v(37.65, -15.29) * mm});
            skLineSegment(sketch, "E385.MirrorCS", {"start": v(16.85, -34.02) * mm, "end": v(17.46, -36.69) * mm});
            skArc(sketch, "E386.MirrorCS", {"start": v(16.15, -33.66) * mm, "mid": v(16.58, -33.68) * mm, "end": v(16.85, -34.02) * mm});
            skLineSegment(sketch, "E387.MirrorCS", {"start": v(27.75, -25.07) * mm, "end": v(29.06, -23.64) * mm});
            skLineSegment(sketch, "E388.MirrorCS", {"start": v(33.84, -15.67) * mm, "end": v(34.66, -13.92) * mm});
            skLineSegment(sketch, "E389.MirrorCS", {"start": v(-26.6, -31.39) * mm, "end": v(-27.35, -30.75) * mm});
            skLineSegment(sketch, "E390.MirrorCS", {"start": v(-31.25, -20.8) * mm, "end": v(-32.23, -19.13) * mm});
            skLineSegment(sketch, "E391.MirrorCS", {"start": v(3.43, -37.2) * mm, "end": v(5.36, -36.95) * mm});
            skLineSegment(sketch, "E392.MirrorCS", {"start": v(-35.4, -13.71) * mm, "end": v(-37.65, -15.29) * mm});
            skLineSegment(sketch, "E393.MirrorCS", {"start": v(-39.02, -11.15) * mm, "end": v(-36.28, -10.93) * mm});
            skLineSegment(sketch, "E394.MirrorCS", {"start": v(-3.84, -40.48) * mm, "end": v(-3.01, -37.86) * mm});
            skLineSegment(sketch, "E395.MirrorCS", {"start": v(-11.5, -36.2) * mm, "end": v(-11.84, -38.93) * mm});
            skLineSegment(sketch, "E396.MirrorCS", {"start": v(-30.16, -27.32) * mm, "end": v(-27.85, -25.84) * mm});
            skLineSegment(sketch, "E397.MirrorCS", {"start": v(-16.85, -34.02) * mm, "end": v(-17.46, -36.69) * mm});
            skLineSegment(sketch, "E398.MirrorCS", {"start": v(-5.93, -37.48) * mm, "end": v(-5.8, -40.22) * mm});
            skLineSegment(sketch, "E399.MirrorCS", {"start": v(-37.02, -8.09) * mm, "end": v(-39.52, -9.23) * mm});
            skPoint(sketch, "E400.MirrorP", {"position": v(17.56, -37.1) * mm});
            skPoint(sketch, "E401.MirrorP", {"position": v(-35.68, -10.88) * mm});
            skPoint(sketch, "E402.MirrorP", {"position": v(-37.1, -5.4) * mm});
            skPoint(sketch, "E403.MirrorP", {"position": v(3.96, -40.88) * mm});
            skPoint(sketch, "E404.MirrorP", {"position": v(-30.94, -21.32) * mm});
            skPoint(sketch, "E405.MirrorP", {"position": v(15.87, -37.82) * mm});
            skPoint(sketch, "E406.MirrorP", {"position": v(26.28, -31.66) * mm});
            skPoint(sketch, "E407.MirrorP", {"position": v(40.87, -5.25) * mm});
            skPoint(sketch, "E408.MirrorP", {"position": v(34.48, -22.63) * mm});
            skPoint(sketch, "E409.MirrorP", {"position": v(-33.58, -16.22) * mm});
            skPoint(sketch, "E410.MirrorP", {"position": v(-16.71, -33.43) * mm});
            skPoint(sketch, "E411.MirrorP", {"position": v(11.89, -39.35) * mm});
            skPoint(sketch, "E412.MirrorP", {"position": v(23.02, -34.05) * mm});
            skPoint(sketch, "E413.MirrorP", {"position": v(31.76, -26.2) * mm});
            skPoint(sketch, "E414.MirrorP", {"position": v(39.9, -9.4) * mm});
            skPoint(sketch, "E415.MirrorP", {"position": v(38, -15.53) * mm});
            skPoint(sketch, "E416.MirrorP", {"position": v(-23.36, -29.26) * mm});
            skPoint(sketch, "E417.MirrorP", {"position": v(-2.83, -37.28) * mm});
            skPoint(sketch, "E418.MirrorP", {"position": v(-40.87, -5.25) * mm});
            skPoint(sketch, "E419.MirrorP", {"position": v(-34.91, -13.37) * mm});
            skPoint(sketch, "E420.MirrorP", {"position": v(33.58, -16.22) * mm});
            skPoint(sketch, "E421.MirrorP", {"position": v(27.34, -25.51) * mm});
            skPoint(sketch, "E422.MirrorP", {"position": v(18.9, -32.28) * mm});
            skPoint(sketch, "E423.MirrorP", {"position": v(35.68, -10.88) * mm});
            skPoint(sketch, "E424.MirrorP", {"position": v(-10.13, -39.9) * mm});
            skPoint(sketch, "E425.MirrorP", {"position": v(-29.47, -23.2) * mm});
            skPoint(sketch, "E426.MirrorP", {"position": v(11.42, -35.6) * mm});
            skPoint(sketch, "E427.MirrorP", {"position": v(29.47, -23.2) * mm});
            skPoint(sketch, "E428.MirrorP", {"position": v(21.55, -30.57) * mm});
            skPoint(sketch, "E429.MirrorP", {"position": v(-37.23, -17.2) * mm});
            skPoint(sketch, "E430.MirrorP", {"position": v(-37.52, -2.28) * mm});
            skPoint(sketch, "E431.MirrorP", {"position": v(8.41, -36.53) * mm});
            skPoint(sketch, "E432.MirrorP", {"position": v(36.47, -7.84) * mm});
            skPoint(sketch, "E433.MirrorP", {"position": v(34.91, -13.37) * mm});
            skPoint(sketch, "E434.MirrorP", {"position": v(39.44, -11.18) * mm});
            skPoint(sketch, "E435.MirrorP", {"position": v(21.47, -35.05) * mm});
            skPoint(sketch, "E436.MirrorP", {"position": v(-39.44, -11.18) * mm});
            skPoint(sketch, "E437.MirrorP", {"position": v(-21.55, -30.57) * mm});
            skPoint(sketch, "E438.MirrorP", {"position": v(30.52, -27.55) * mm});
            skPoint(sketch, "E439.MirrorP", {"position": v(37.23, -17.2) * mm});
            skPoint(sketch, "E440.MirrorP", {"position": v(10.13, -39.9) * mm});
            skPoint(sketch, "E441.MirrorP", {"position": v(-17.56, -37.1) * mm});
            skPoint(sketch, "E442.MirrorP", {"position": v(-35.41, -21.04) * mm});
            skPoint(sketch, "E443.MirrorP", {"position": v(-27.34, -25.51) * mm});
            skPoint(sketch, "E444.MirrorP", {"position": v(-11.42, -35.6) * mm});
            skPoint(sketch, "E445.MirrorP", {"position": v(-34.48, -22.63) * mm});
            skPoint(sketch, "E446.MirrorP", {"position": v(-5.96, -36.88) * mm});
            skPoint(sketch, "E447.MirrorP", {"position": v(2.83, -37.28) * mm});
            skPoint(sketch, "E448.MirrorP", {"position": v(-26.28, -31.66) * mm});
            skPoint(sketch, "E449.MirrorP", {"position": v(-18.9, -32.28) * mm});
            skPoint(sketch, "E450.MirrorP", {"position": v(-36.47, -7.84) * mm});
            skPoint(sketch, "E451.MirrorP", {"position": v(-8.41, -36.53) * mm});
            skPoint(sketch, "E452.MirrorP", {"position": v(5.96, -36.88) * mm});
            skPoint(sketch, "E453.MirrorP", {"position": v(-13.81, -34.66) * mm});
            skPoint(sketch, "E454.MirrorP", {"position": v(-41.11, -3.43) * mm});
            skPoint(sketch, "E455.MirrorP", {"position": v(-25.76, -27.22) * mm});
            skPoint(sketch, "E456.MirrorP", {"position": v(-3.96, -40.88) * mm});
            skPoint(sketch, "E457.MirrorP", {"position": v(-11.89, -39.35) * mm});
            skPoint(sketch, "E458.MirrorP", {"position": v(-38, -15.53) * mm});
            skPoint(sketch, "E459.MirrorP", {"position": v(30.94, -21.32) * mm});
            skPoint(sketch, "E460.MirrorP", {"position": v(-27.67, -30.47) * mm});
            skPoint(sketch, "E461.MirrorP", {"position": v(16.71, -33.43) * mm});
            skPoint(sketch, "E462.MirrorP", {"position": v(32.53, -18.6) * mm});
            skPoint(sketch, "E463.MirrorP", {"position": v(-39.9, -9.4) * mm});
            skPoint(sketch, "E464.MirrorP", {"position": v(35.41, -21.04) * mm});
            skPoint(sketch, "E465.MirrorP", {"position": v(41.11, -3.43) * mm});
            skPoint(sketch, "E466.MirrorP", {"position": v(23.36, -29.26) * mm});
            skPoint(sketch, "E467.MirrorP", {"position": v(-30.52, -27.55) * mm});
            skPoint(sketch, "E468.MirrorP", {"position": v(-23.02, -34.05) * mm});
            skPoint(sketch, "E469.MirrorP", {"position": v(-15.87, -37.82) * mm});
            skPoint(sketch, "E470.MirrorP", {"position": v(37.1, -5.4) * mm});
            skPoint(sketch, "E471.MirrorP", {"position": v(5.79, -40.65) * mm});
            skPoint(sketch, "E472.MirrorP", {"position": v(27.67, -30.47) * mm});
            skPoint(sketch, "E473.MirrorP", {"position": v(-32.53, -18.6) * mm});
            skPoint(sketch, "E474.MirrorP", {"position": v(-21.47, -35.05) * mm});
            skPoint(sketch, "E475.MirrorP", {"position": v(25.76, -27.22) * mm});
            skPoint(sketch, "E476.MirrorP", {"position": v(37.52, -2.28) * mm});
            skPoint(sketch, "E477.MirrorP", {"position": v(-31.76, -26.2) * mm});
            skPoint(sketch, "E478.MirrorP", {"position": v(13.81, -34.66) * mm});
            skPoint(sketch, "E479.MirrorP", {"position": v(-5.79, -40.65) * mm});
            skSolve(sketch);
        }
        {
            var Q0;
            Q0=makeQuery(id+"F0.imprint","IMPRINT",FACE,{"disambiguationData":[TD([[makeQuery(id+"F0.imprint","IMPRINT",EDGE,{"derivedFrom":sQuery(id+"F0.wireOp",EDGE,"E1")}),-1.0]])]});
            var sketch = newSketch(context, id + "F1", { "sketchPlane" : qUnion([Q0])});
            skCircle(sketch, "E480", {"center": v(-66.74, 50.33) * mm, "radius": 19.05 * mm});
            skCircle(sketch, "E481", {"center": v(-66.74, 50.33) * mm, "radius": 6.35 * mm});
            skLineSegment(sketch, "E482", {"start": v(-66.74, 69.38) * mm, "end": v(-66.74, 31.28) * mm, "construction": true});
            skLineSegment(sketch, "E483", {"start": v(-85.79, 50.33) * mm, "end": v(-47.69, 50.33) * mm, "construction": true});
            skLineSegment(sketch, "E484", {"start": v(-48.65, 53.87) * mm, "end": v(-48.48, 51.94) * mm});
            skLineSegment(sketch, "E485", {"start": v(-45.37, 54.19) * mm, "end": v(-48.1, 54.43) * mm});
            skLineSegment(sketch, "E486", {"start": v(-47.84, 51.5) * mm, "end": v(-45.2, 52.2) * mm});
            skLineSegment(sketch, "E487", {"start": v(-44.9, 53.72) * mm, "end": v(-44.82, 52.74) * mm});
            skPoint(sketch, "E488.visualSharp", {"position": v(-44.94, 54.15) * mm});
            skArc(sketch, "E488.filletArc", {"start": v(-44.9, 53.72) * mm, "mid": v(-45.05, 54.04) * mm, "end": v(-45.37, 54.19) * mm});
            skPoint(sketch, "E489.visualSharp", {"position": v(-48.7, 54.48) * mm});
            skArc(sketch, "E489.filletArc", {"start": v(-48.1, 54.43) * mm, "mid": v(-48.5, 54.28) * mm, "end": v(-48.65, 53.87) * mm});
            skPoint(sketch, "E490.visualSharp", {"position": v(-48.43, 51.34) * mm});
            skArc(sketch, "E490.filletArc", {"start": v(-48.48, 51.94) * mm, "mid": v(-48.26, 51.57) * mm, "end": v(-47.84, 51.5) * mm});
            skPoint(sketch, "E491.visualSharp", {"position": v(-44.78, 52.32) * mm});
            skArc(sketch, "E491.filletArc", {"start": v(-45.2, 52.2) * mm, "mid": v(-44.9, 52.4) * mm, "end": v(-44.82, 52.74) * mm});
            skLineSegment(sketch, "E492.0", {"start": v(-44.78, 52.32) * mm, "end": v(-44.94, 54.15) * mm, "construction": true});
            skLineSegment(sketch, "E493", {"start": v(-51, 59.36) * mm, "end": v(-50.05, 57.67) * mm});
            skLineSegment(sketch, "E494", {"start": v(-48.14, 61) * mm, "end": v(-50.73, 60.09) * mm});
            skLineSegment(sketch, "E495", {"start": v(-49.29, 57.53) * mm, "end": v(-47.17, 59.26) * mm});
            skLineSegment(sketch, "E496", {"start": v(-47.53, 60.76) * mm, "end": v(-47.05, 59.9) * mm});
            skPoint(sketch, "E497.visualSharp", {"position": v(-47.74, 61.14) * mm});
            skArc(sketch, "E497.filletArc", {"start": v(-47.53, 60.76) * mm, "mid": v(-47.8, 61) * mm, "end": v(-48.14, 61) * mm});
            skPoint(sketch, "E498.visualSharp", {"position": v(-51.3, 59.89) * mm});
            skArc(sketch, "E498.filletArc", {"start": v(-50.73, 60.09) * mm, "mid": v(-51.04, 59.79) * mm, "end": v(-51, 59.36) * mm});
            skPoint(sketch, "E499.visualSharp", {"position": v(-49.76, 57.14) * mm});
            skArc(sketch, "E499.filletArc", {"start": v(-50.05, 57.67) * mm, "mid": v(-49.7, 57.42) * mm, "end": v(-49.29, 57.53) * mm});
            skPoint(sketch, "E500.visualSharp", {"position": v(-46.84, 59.53) * mm});
            skArc(sketch, "E500.filletArc", {"start": v(-47.17, 59.26) * mm, "mid": v(-47, 59.56) * mm, "end": v(-47.05, 59.9) * mm});
            skLineSegment(sketch, "E501.0", {"start": v(-46.84, 59.53) * mm, "end": v(-47.74, 61.14) * mm, "construction": true});
            skLineSegment(sketch, "E502", {"start": v(-54.76, 64.14) * mm, "end": v(-53.39, 62.77) * mm});
            skLineSegment(sketch, "E503", {"start": v(-52.44, 66.5) * mm, "end": v(-54.69, 64.92) * mm});
            skLineSegment(sketch, "E504", {"start": v(-52.6, 62.84) * mm, "end": v(-51.04, 65.09) * mm});
            skLineSegment(sketch, "E505", {"start": v(-51.8, 66.43) * mm, "end": v(-51.1, 65.74) * mm});
            skPoint(sketch, "E506.visualSharp", {"position": v(-52.1, 66.74) * mm});
            skArc(sketch, "E506.filletArc", {"start": v(-51.8, 66.43) * mm, "mid": v(-52.1, 66.58) * mm, "end": v(-52.44, 66.5) * mm});
            skPoint(sketch, "E507.visualSharp", {"position": v(-55.18, 64.57) * mm});
            skArc(sketch, "E507.filletArc", {"start": v(-54.69, 64.92) * mm, "mid": v(-54.9, 64.55) * mm, "end": v(-54.76, 64.14) * mm});
            skPoint(sketch, "E508.visualSharp", {"position": v(-52.96, 62.34) * mm});
            skArc(sketch, "E508.filletArc", {"start": v(-53.39, 62.77) * mm, "mid": v(-52.98, 62.63) * mm, "end": v(-52.6, 62.84) * mm});
            skPoint(sketch, "E509.visualSharp", {"position": v(-50.8, 65.43) * mm});
            skArc(sketch, "E509.filletArc", {"start": v(-51.04, 65.09) * mm, "mid": v(-50.95, 65.42) * mm, "end": v(-51.1, 65.74) * mm});
            skLineSegment(sketch, "E510.0", {"start": v(-50.8, 65.43) * mm, "end": v(-52.1, 66.74) * mm, "construction": true});
            skLineSegment(sketch, "E511", {"start": v(-59.34, 67.15) * mm, "end": v(-57.66, 66.18) * mm});
            skLineSegment(sketch, "E512", {"start": v(-57.71, 70.02) * mm, "end": v(-59.47, 67.92) * mm});
            skLineSegment(sketch, "E513", {"start": v(-56.93, 66.45) * mm, "end": v(-56, 69.02) * mm});
            skLineSegment(sketch, "E514", {"start": v(-57.07, 70.13) * mm, "end": v(-56.21, 69.64) * mm});
            skPoint(sketch, "E515.visualSharp", {"position": v(-57.44, 70.34) * mm});
            skArc(sketch, "E515.filletArc", {"start": v(-57.07, 70.13) * mm, "mid": v(-57.41, 70.2) * mm, "end": v(-57.71, 70.02) * mm});
            skPoint(sketch, "E516.visualSharp", {"position": v(-59.86, 67.45) * mm});
            skArc(sketch, "E516.filletArc", {"start": v(-59.47, 67.92) * mm, "mid": v(-59.59, 67.5) * mm, "end": v(-59.34, 67.15) * mm});
            skPoint(sketch, "E517.visualSharp", {"position": v(-57.14, 65.88) * mm});
            skArc(sketch, "E517.filletArc", {"start": v(-57.66, 66.18) * mm, "mid": v(-57.23, 66.14) * mm, "end": v(-56.93, 66.45) * mm});
            skPoint(sketch, "E518.visualSharp", {"position": v(-55.85, 69.42) * mm});
            skArc(sketch, "E518.filletArc", {"start": v(-56, 69.02) * mm, "mid": v(-56, 69.37) * mm, "end": v(-56.21, 69.64) * mm});
            skLineSegment(sketch, "E519.0", {"start": v(-55.85, 69.42) * mm, "end": v(-57.44, 70.34) * mm, "construction": true});
            skLineSegment(sketch, "E520", {"start": v(-64.85, 68.7) * mm, "end": v(-62.95, 68.35) * mm});
            skLineSegment(sketch, "E521", {"start": v(-64.3, 71.94) * mm, "end": v(-65.24, 69.36) * mm});
            skLineSegment(sketch, "E522", {"start": v(-62.35, 68.85) * mm, "end": v(-62.35, 71.6) * mm});
            skLineSegment(sketch, "E523", {"start": v(-63.74, 72.27) * mm, "end": v(-62.77, 72.1) * mm});
            skPoint(sketch, "E524.visualSharp", {"position": v(-64.16, 72.34) * mm});
            skArc(sketch, "E524.filletArc", {"start": v(-63.74, 72.27) * mm, "mid": v(-64.08, 72.2) * mm, "end": v(-64.3, 71.94) * mm});
            skPoint(sketch, "E525.visualSharp", {"position": v(-65.45, 68.8) * mm});
            skArc(sketch, "E525.filletArc", {"start": v(-65.24, 69.36) * mm, "mid": v(-65.2, 68.94) * mm, "end": v(-64.85, 68.7) * mm});
            skPoint(sketch, "E526.visualSharp", {"position": v(-62.35, 68.25) * mm});
            skArc(sketch, "E526.filletArc", {"start": v(-62.95, 68.35) * mm, "mid": v(-62.53, 68.47) * mm, "end": v(-62.35, 68.85) * mm});
            skPoint(sketch, "E527.visualSharp", {"position": v(-62.35, 72.02) * mm});
            skArc(sketch, "E527.filletArc", {"start": v(-62.35, 71.6) * mm, "mid": v(-62.47, 71.92) * mm, "end": v(-62.77, 72.1) * mm});
            skLineSegment(sketch, "E528.0", {"start": v(-62.35, 72.02) * mm, "end": v(-64.16, 72.34) * mm, "construction": true});
            skLineSegment(sketch, "E529.MirrorCS", {"start": v(-69.73, 72.27) * mm, "end": v(-70.7, 72.1) * mm});
            skArc(sketch, "E530.MirrorCS", {"start": v(-69.73, 72.27) * mm, "mid": v(-69.39, 72.2) * mm, "end": v(-69.17, 71.94) * mm});
            skLineSegment(sketch, "E531.MirrorCS", {"start": v(-88.7, 52.32) * mm, "end": v(-88.53, 54.15) * mm, "construction": true});
            skArc(sketch, "E532.MirrorCS", {"start": v(-71.12, 71.6) * mm, "mid": v(-71, 71.92) * mm, "end": v(-70.7, 72.1) * mm});
            skLineSegment(sketch, "E533.MirrorCS", {"start": v(-88.57, 53.72) * mm, "end": v(-88.65, 52.74) * mm});
            skArc(sketch, "E534.MirrorCS", {"start": v(-76.4, 70.13) * mm, "mid": v(-76.06, 70.2) * mm, "end": v(-75.76, 70.02) * mm});
            skArc(sketch, "E535.MirrorCS", {"start": v(-78.78, 64.92) * mm, "mid": v(-78.57, 64.55) * mm, "end": v(-78.72, 64.14) * mm});
            skArc(sketch, "E536.MirrorCS", {"start": v(-83.42, 57.67) * mm, "mid": v(-83.77, 57.42) * mm, "end": v(-84.18, 57.53) * mm});
            skArc(sketch, "E537.MirrorCS", {"start": v(-81.68, 66.43) * mm, "mid": v(-81.37, 66.58) * mm, "end": v(-81.03, 66.5) * mm});
            skLineSegment(sketch, "E538.MirrorCS", {"start": v(-76.4, 70.13) * mm, "end": v(-77.26, 69.64) * mm});
            skArc(sketch, "E539.MirrorCS", {"start": v(-82.44, 65.09) * mm, "mid": v(-82.53, 65.42) * mm, "end": v(-82.38, 65.74) * mm});
            skArc(sketch, "E540.MirrorCS", {"start": v(-86.3, 59.26) * mm, "mid": v(-86.48, 59.56) * mm, "end": v(-86.43, 59.9) * mm});
            skArc(sketch, "E541.MirrorCS", {"start": v(-75.81, 66.18) * mm, "mid": v(-76.24, 66.14) * mm, "end": v(-76.54, 66.45) * mm});
            skArc(sketch, "E542.MirrorCS", {"start": v(-74, 67.92) * mm, "mid": v(-73.89, 67.5) * mm, "end": v(-74.13, 67.15) * mm});
            skArc(sketch, "E543.MirrorCS", {"start": v(-80.09, 62.77) * mm, "mid": v(-80.5, 62.63) * mm, "end": v(-80.86, 62.84) * mm});
            skArc(sketch, "E544.MirrorCS", {"start": v(-82.74, 60.09) * mm, "mid": v(-82.44, 59.79) * mm, "end": v(-82.47, 59.36) * mm});
            skLineSegment(sketch, "E545.MirrorCS", {"start": v(-81.68, 66.43) * mm, "end": v(-82.38, 65.74) * mm});
            skArc(sketch, "E546.MirrorCS", {"start": v(-88.28, 52.2) * mm, "mid": v(-88.56, 52.4) * mm, "end": v(-88.65, 52.74) * mm});
            skLineSegment(sketch, "E547.MirrorCS", {"start": v(-82.68, 65.43) * mm, "end": v(-81.38, 66.74) * mm, "construction": true});
            skLineSegment(sketch, "E548.MirrorCS", {"start": v(-71.12, 72.02) * mm, "end": v(-69.31, 72.34) * mm, "construction": true});
            skArc(sketch, "E549.MirrorCS", {"start": v(-85.94, 60.76) * mm, "mid": v(-85.68, 61) * mm, "end": v(-85.33, 61) * mm});
            skArc(sketch, "E550.MirrorCS", {"start": v(-77.48, 69.02) * mm, "mid": v(-77.48, 69.37) * mm, "end": v(-77.26, 69.64) * mm});
            skArc(sketch, "E551.MirrorCS", {"start": v(-68.23, 69.36) * mm, "mid": v(-68.27, 68.94) * mm, "end": v(-68.62, 68.7) * mm});
            skLineSegment(sketch, "E552.MirrorCS", {"start": v(-85.94, 60.76) * mm, "end": v(-86.43, 59.9) * mm});
            skArc(sketch, "E553.MirrorCS", {"start": v(-85, 51.94) * mm, "mid": v(-85.2, 51.57) * mm, "end": v(-85.63, 51.5) * mm});
            skLineSegment(sketch, "E554.MirrorCS", {"start": v(-86.63, 59.53) * mm, "end": v(-85.73, 61.14) * mm, "construction": true});
            skLineSegment(sketch, "E555.MirrorCS", {"start": v(-77.63, 69.42) * mm, "end": v(-76.04, 70.34) * mm, "construction": true});
            skArc(sketch, "E556.MirrorCS", {"start": v(-70.53, 68.35) * mm, "mid": v(-70.94, 68.47) * mm, "end": v(-71.12, 68.85) * mm});
            skArc(sketch, "E557.MirrorCS", {"start": v(-88.57, 53.72) * mm, "mid": v(-88.42, 54.04) * mm, "end": v(-88.1, 54.19) * mm});
            skArc(sketch, "E558.MirrorCS", {"start": v(-85.38, 54.43) * mm, "mid": v(-84.97, 54.28) * mm, "end": v(-84.82, 53.87) * mm});
            skPoint(sketch, "E559.MirrorP", {"position": v(-85.05, 51.34) * mm});
            skPoint(sketch, "E560.MirrorP", {"position": v(-80.52, 62.34) * mm});
            skPoint(sketch, "E561.MirrorP", {"position": v(-76.34, 65.88) * mm});
            skPoint(sketch, "E562.MirrorP", {"position": v(-68.02, 68.8) * mm});
            skPoint(sketch, "E563.MirrorP", {"position": v(-82.17, 59.89) * mm});
            skPoint(sketch, "E564.MirrorP", {"position": v(-86.63, 59.53) * mm});
            skPoint(sketch, "E565.MirrorP", {"position": v(-71.12, 72.02) * mm});
            skLineSegment(sketch, "E566.MirrorCS", {"start": v(-74.13, 67.15) * mm, "end": v(-75.81, 66.18) * mm});
            skLineSegment(sketch, "E567.MirrorCS", {"start": v(-71.12, 68.85) * mm, "end": v(-71.12, 71.6) * mm});
            skLineSegment(sketch, "E568.MirrorCS", {"start": v(-76.54, 66.45) * mm, "end": v(-77.48, 69.02) * mm});
            skLineSegment(sketch, "E569.MirrorCS", {"start": v(-81.03, 66.5) * mm, "end": v(-78.78, 64.92) * mm});
            skLineSegment(sketch, "E570.MirrorCS", {"start": v(-75.76, 70.02) * mm, "end": v(-74, 67.92) * mm});
            skLineSegment(sketch, "E571.MirrorCS", {"start": v(-84.18, 57.53) * mm, "end": v(-86.3, 59.26) * mm});
            skLineSegment(sketch, "E572.MirrorCS", {"start": v(-80.86, 62.84) * mm, "end": v(-82.44, 65.09) * mm});
            skPoint(sketch, "E573.MirrorP", {"position": v(-88.7, 52.32) * mm});
            skPoint(sketch, "E574.MirrorP", {"position": v(-82.68, 65.43) * mm});
            skLineSegment(sketch, "E575.MirrorCS", {"start": v(-85.33, 61) * mm, "end": v(-82.74, 60.09) * mm});
            skPoint(sketch, "E576.MirrorP", {"position": v(-77.63, 69.42) * mm});
            skPoint(sketch, "E577.MirrorP", {"position": v(-69.31, 72.34) * mm});
            skLineSegment(sketch, "E578.MirrorCS", {"start": v(-82.47, 59.36) * mm, "end": v(-83.42, 57.67) * mm});
            skLineSegment(sketch, "E579.MirrorCS", {"start": v(-88.1, 54.19) * mm, "end": v(-85.38, 54.43) * mm});
            skLineSegment(sketch, "E580.MirrorCS", {"start": v(-84.82, 53.87) * mm, "end": v(-85, 51.94) * mm});
            skLineSegment(sketch, "E581.MirrorCS", {"start": v(-85.63, 51.5) * mm, "end": v(-88.28, 52.2) * mm});
            skPoint(sketch, "E582.MirrorP", {"position": v(-71.12, 68.25) * mm});
            skPoint(sketch, "E583.MirrorP", {"position": v(-85.73, 61.14) * mm});
            skLineSegment(sketch, "E584.MirrorCS", {"start": v(-78.72, 64.14) * mm, "end": v(-80.09, 62.77) * mm});
            skPoint(sketch, "E585.MirrorP", {"position": v(-83.72, 57.14) * mm});
            skPoint(sketch, "E586.MirrorP", {"position": v(-76.04, 70.34) * mm});
            skLineSegment(sketch, "E587.MirrorCS", {"start": v(-68.62, 68.7) * mm, "end": v(-70.53, 68.35) * mm});
            skLineSegment(sketch, "E588.MirrorCS", {"start": v(-69.17, 71.94) * mm, "end": v(-68.23, 69.36) * mm});
            skPoint(sketch, "E589.MirrorP", {"position": v(-84.77, 54.48) * mm});
            skPoint(sketch, "E590.MirrorP", {"position": v(-78.29, 64.57) * mm});
            skPoint(sketch, "E591.MirrorP", {"position": v(-73.6, 67.45) * mm});
            skPoint(sketch, "E592.MirrorP", {"position": v(-88.53, 54.15) * mm});
            skPoint(sketch, "E593.MirrorP", {"position": v(-81.38, 66.74) * mm});
            skLineSegment(sketch, "E594.MirrorCS", {"start": v(-47.53, 39.9) * mm, "end": v(-47.05, 40.75) * mm});
            skArc(sketch, "E595.MirrorCS", {"start": v(-51.8, 34.22) * mm, "mid": v(-52.1, 34.08) * mm, "end": v(-52.44, 34.17) * mm});
            skLineSegment(sketch, "E596.MirrorCS", {"start": v(-57.07, 30.53) * mm, "end": v(-56.21, 31.02) * mm});
            skArc(sketch, "E597.MirrorCS", {"start": v(-69.73, 28.4) * mm, "mid": v(-69.39, 28.45) * mm, "end": v(-69.17, 28.72) * mm});
            skArc(sketch, "E598.MirrorCS", {"start": v(-88.28, 48.45) * mm, "mid": v(-88.56, 48.25) * mm, "end": v(-88.65, 47.92) * mm});
            skLineSegment(sketch, "E599.MirrorCS", {"start": v(-51.8, 34.22) * mm, "end": v(-51.1, 34.92) * mm});
            skLineSegment(sketch, "E600.MirrorCS", {"start": v(-81.68, 34.22) * mm, "end": v(-82.38, 34.92) * mm});
            skArc(sketch, "E601.MirrorCS", {"start": v(-45.2, 48.45) * mm, "mid": v(-44.9, 48.25) * mm, "end": v(-44.82, 47.92) * mm});
            skArc(sketch, "E602.MirrorCS", {"start": v(-48.48, 48.71) * mm, "mid": v(-48.26, 49.09) * mm, "end": v(-47.84, 49.16) * mm});
            skArc(sketch, "E603.MirrorCS", {"start": v(-48.1, 46.23) * mm, "mid": v(-48.5, 46.38) * mm, "end": v(-48.65, 46.78) * mm});
            skArc(sketch, "E604.MirrorCS", {"start": v(-44.9, 46.93) * mm, "mid": v(-45.05, 46.62) * mm, "end": v(-45.37, 46.47) * mm});
            skLineSegment(sketch, "E605.MirrorCS", {"start": v(-44.9, 46.93) * mm, "end": v(-44.82, 47.92) * mm});
            skArc(sketch, "E606.MirrorCS", {"start": v(-82.74, 40.57) * mm, "mid": v(-82.44, 40.87) * mm, "end": v(-82.47, 41.3) * mm});
            skArc(sketch, "E607.MirrorCS", {"start": v(-62.35, 29.06) * mm, "mid": v(-62.47, 28.74) * mm, "end": v(-62.77, 28.56) * mm});
            skArc(sketch, "E608.MirrorCS", {"start": v(-80.09, 37.89) * mm, "mid": v(-80.5, 38.03) * mm, "end": v(-80.86, 37.82) * mm});
            skArc(sketch, "E609.MirrorCS", {"start": v(-62.95, 32.3) * mm, "mid": v(-62.53, 32.2) * mm, "end": v(-62.35, 31.8) * mm});
            skArc(sketch, "E610.MirrorCS", {"start": v(-74, 32.74) * mm, "mid": v(-73.89, 33.16) * mm, "end": v(-74.13, 33.5) * mm});
            skArc(sketch, "E611.MirrorCS", {"start": v(-85.38, 46.23) * mm, "mid": v(-84.97, 46.38) * mm, "end": v(-84.82, 46.78) * mm});
            skArc(sketch, "E612.MirrorCS", {"start": v(-65.24, 31.3) * mm, "mid": v(-65.2, 31.72) * mm, "end": v(-64.85, 31.97) * mm});
            skArc(sketch, "E613.MirrorCS", {"start": v(-75.81, 34.48) * mm, "mid": v(-76.24, 34.51) * mm, "end": v(-76.54, 34.21) * mm});
            skArc(sketch, "E614.MirrorCS", {"start": v(-88.57, 46.93) * mm, "mid": v(-88.42, 46.62) * mm, "end": v(-88.1, 46.47) * mm});
            skLineSegment(sketch, "E615.MirrorCS", {"start": v(-46.84, 41.12) * mm, "end": v(-47.74, 39.52) * mm, "construction": true});
            skLineSegment(sketch, "E616.MirrorCS", {"start": v(-82.68, 35.22) * mm, "end": v(-81.38, 33.92) * mm, "construction": true});
            skArc(sketch, "E617.MirrorCS", {"start": v(-57.07, 30.53) * mm, "mid": v(-57.41, 30.47) * mm, "end": v(-57.71, 30.64) * mm});
            skArc(sketch, "E618.MirrorCS", {"start": v(-54.69, 35.74) * mm, "mid": v(-54.9, 36.11) * mm, "end": v(-54.76, 36.52) * mm});
            skArc(sketch, "E619.MirrorCS", {"start": v(-51.04, 35.57) * mm, "mid": v(-50.95, 35.24) * mm, "end": v(-51.1, 34.92) * mm});
            skArc(sketch, "E620.MirrorCS", {"start": v(-85.94, 39.9) * mm, "mid": v(-85.68, 39.67) * mm, "end": v(-85.33, 39.66) * mm});
            skArc(sketch, "E621.MirrorCS", {"start": v(-57.66, 34.48) * mm, "mid": v(-57.23, 34.51) * mm, "end": v(-56.93, 34.21) * mm});
            skArc(sketch, "E622.MirrorCS", {"start": v(-47.53, 39.9) * mm, "mid": v(-47.8, 39.67) * mm, "end": v(-48.14, 39.66) * mm});
            skArc(sketch, "E623.MirrorCS", {"start": v(-81.68, 34.22) * mm, "mid": v(-81.37, 34.08) * mm, "end": v(-81.03, 34.17) * mm});
            skArc(sketch, "E624.MirrorCS", {"start": v(-63.74, 28.4) * mm, "mid": v(-64.08, 28.45) * mm, "end": v(-64.3, 28.72) * mm});
            skArc(sketch, "E625.MirrorCS", {"start": v(-86.3, 41.4) * mm, "mid": v(-86.48, 41.1) * mm, "end": v(-86.43, 40.75) * mm});
            skArc(sketch, "E626.MirrorCS", {"start": v(-47.17, 41.4) * mm, "mid": v(-47, 41.1) * mm, "end": v(-47.05, 40.75) * mm});
            skArc(sketch, "E627.MirrorCS", {"start": v(-85, 48.71) * mm, "mid": v(-85.2, 49.09) * mm, "end": v(-85.63, 49.16) * mm});
            skArc(sketch, "E628.MirrorCS", {"start": v(-50.73, 40.57) * mm, "mid": v(-51.04, 40.87) * mm, "end": v(-51, 41.3) * mm});
            skArc(sketch, "E629.MirrorCS", {"start": v(-50.05, 42.99) * mm, "mid": v(-49.7, 43.24) * mm, "end": v(-49.29, 43.13) * mm});
            skLineSegment(sketch, "E630.MirrorCS", {"start": v(-77.63, 31.23) * mm, "end": v(-76.04, 30.31) * mm, "construction": true});
            skArc(sketch, "E631.MirrorCS", {"start": v(-82.44, 35.57) * mm, "mid": v(-82.53, 35.24) * mm, "end": v(-82.38, 34.92) * mm});
            skLineSegment(sketch, "E632.MirrorCS", {"start": v(-86.63, 41.12) * mm, "end": v(-85.73, 39.52) * mm, "construction": true});
            skLineSegment(sketch, "E633.MirrorCS", {"start": v(-76.4, 30.53) * mm, "end": v(-77.26, 31.02) * mm});
            skArc(sketch, "E634.MirrorCS", {"start": v(-76.4, 30.53) * mm, "mid": v(-76.06, 30.47) * mm, "end": v(-75.76, 30.64) * mm});
            skArc(sketch, "E635.MirrorCS", {"start": v(-77.48, 31.63) * mm, "mid": v(-77.48, 31.29) * mm, "end": v(-77.26, 31.02) * mm});
            skArc(sketch, "E636.MirrorCS", {"start": v(-83.42, 42.99) * mm, "mid": v(-83.77, 43.24) * mm, "end": v(-84.18, 43.13) * mm});
            skArc(sketch, "E637.MirrorCS", {"start": v(-56, 31.63) * mm, "mid": v(-56, 31.29) * mm, "end": v(-56.21, 31.02) * mm});
            skArc(sketch, "E638.MirrorCS", {"start": v(-71.12, 29.06) * mm, "mid": v(-71, 28.74) * mm, "end": v(-70.7, 28.56) * mm});
            skArc(sketch, "E639.MirrorCS", {"start": v(-68.23, 31.3) * mm, "mid": v(-68.27, 31.72) * mm, "end": v(-68.62, 31.97) * mm});
            skLineSegment(sketch, "E640.MirrorCS", {"start": v(-63.74, 28.4) * mm, "end": v(-62.77, 28.56) * mm});
            skArc(sketch, "E641.MirrorCS", {"start": v(-53.39, 37.89) * mm, "mid": v(-52.98, 38.03) * mm, "end": v(-52.6, 37.82) * mm});
            skLineSegment(sketch, "E642.MirrorCS", {"start": v(-85.94, 39.9) * mm, "end": v(-86.43, 40.75) * mm});
            skArc(sketch, "E643.MirrorCS", {"start": v(-59.47, 32.74) * mm, "mid": v(-59.59, 33.16) * mm, "end": v(-59.34, 33.5) * mm});
            skLineSegment(sketch, "E644.MirrorCS", {"start": v(-50.8, 35.22) * mm, "end": v(-52.1, 33.92) * mm, "construction": true});
            skArc(sketch, "E645.MirrorCS", {"start": v(-78.78, 35.74) * mm, "mid": v(-78.57, 36.11) * mm, "end": v(-78.72, 36.52) * mm});
            skLineSegment(sketch, "E646.MirrorCS", {"start": v(-55.85, 31.23) * mm, "end": v(-57.44, 30.31) * mm, "construction": true});
            skLineSegment(sketch, "E647.MirrorCS", {"start": v(-44.78, 48.34) * mm, "end": v(-44.94, 46.5) * mm, "construction": true});
            skLineSegment(sketch, "E648.MirrorCS", {"start": v(-69.73, 28.4) * mm, "end": v(-70.7, 28.56) * mm});
            skLineSegment(sketch, "E649.MirrorCS", {"start": v(-62.35, 28.64) * mm, "end": v(-64.16, 28.32) * mm, "construction": true});
            skLineSegment(sketch, "E650.MirrorCS", {"start": v(-88.57, 46.93) * mm, "end": v(-88.65, 47.92) * mm});
            skArc(sketch, "E651.MirrorCS", {"start": v(-70.53, 32.3) * mm, "mid": v(-70.94, 32.2) * mm, "end": v(-71.12, 31.8) * mm});
            skPoint(sketch, "E652.MirrorP", {"position": v(-44.94, 46.5) * mm});
            skPoint(sketch, "E653.MirrorP", {"position": v(-52.1, 33.92) * mm});
            skPoint(sketch, "E654.MirrorP", {"position": v(-57.44, 30.31) * mm});
            skLineSegment(sketch, "E655.MirrorCS", {"start": v(-81.03, 34.17) * mm, "end": v(-78.78, 35.74) * mm});
            skPoint(sketch, "E656.MirrorP", {"position": v(-85.73, 39.52) * mm});
            skLineSegment(sketch, "E657.MirrorCS", {"start": v(-76.54, 34.21) * mm, "end": v(-77.48, 31.63) * mm});
            skLineSegment(sketch, "E658.MirrorCS", {"start": v(-56.93, 34.21) * mm, "end": v(-56, 31.63) * mm});
            skPoint(sketch, "E659.MirrorP", {"position": v(-71.12, 32.4) * mm});
            skLineSegment(sketch, "E660.MirrorCS", {"start": v(-47.84, 49.16) * mm, "end": v(-45.2, 48.45) * mm});
            skLineSegment(sketch, "E661.MirrorCS", {"start": v(-45.37, 46.47) * mm, "end": v(-48.1, 46.23) * mm});
            skLineSegment(sketch, "E662.MirrorCS", {"start": v(-48.65, 46.78) * mm, "end": v(-48.48, 48.71) * mm});
            skLineSegment(sketch, "E663.MirrorCS", {"start": v(-49.29, 43.13) * mm, "end": v(-47.17, 41.4) * mm});
            skLineSegment(sketch, "E664.MirrorCS", {"start": v(-48.14, 39.66) * mm, "end": v(-50.73, 40.57) * mm});
            skLineSegment(sketch, "E665.MirrorCS", {"start": v(-51, 41.3) * mm, "end": v(-50.05, 42.99) * mm});
            skLineSegment(sketch, "E666.MirrorCS", {"start": v(-71.12, 31.8) * mm, "end": v(-71.12, 29.06) * mm});
            skLineSegment(sketch, "E667.MirrorCS", {"start": v(-52.6, 37.82) * mm, "end": v(-51.04, 35.57) * mm});
            skLineSegment(sketch, "E668.MirrorCS", {"start": v(-57.71, 30.64) * mm, "end": v(-59.47, 32.74) * mm});
            skPoint(sketch, "E669.MirrorP", {"position": v(-69.31, 28.32) * mm});
            skPoint(sketch, "E670.MirrorP", {"position": v(-46.84, 41.12) * mm});
            skPoint(sketch, "E671.MirrorP", {"position": v(-62.35, 28.64) * mm});
            skLineSegment(sketch, "E672.MirrorCS", {"start": v(-74.13, 33.5) * mm, "end": v(-75.81, 34.48) * mm});
            skLineSegment(sketch, "E673.MirrorCS", {"start": v(-52.44, 34.17) * mm, "end": v(-54.69, 35.74) * mm});
            skLineSegment(sketch, "E674.MirrorCS", {"start": v(-59.34, 33.5) * mm, "end": v(-57.66, 34.48) * mm});
            skPoint(sketch, "E675.MirrorP", {"position": v(-77.63, 31.23) * mm});
            skLineSegment(sketch, "E676.MirrorCS", {"start": v(-54.76, 36.52) * mm, "end": v(-53.39, 37.89) * mm});
            skPoint(sketch, "E677.MirrorP", {"position": v(-62.35, 32.4) * mm});
            skPoint(sketch, "E678.MirrorP", {"position": v(-82.68, 35.22) * mm});
            skPoint(sketch, "E679.MirrorP", {"position": v(-49.76, 43.52) * mm});
            skLineSegment(sketch, "E680.MirrorCS", {"start": v(-69.17, 28.72) * mm, "end": v(-68.23, 31.3) * mm});
            skPoint(sketch, "E681.MirrorP", {"position": v(-88.7, 48.34) * mm});
            skLineSegment(sketch, "E682.MirrorCS", {"start": v(-88.7, 48.34) * mm, "end": v(-88.53, 46.5) * mm, "construction": true});
            skLineSegment(sketch, "E683.MirrorCS", {"start": v(-75.76, 30.64) * mm, "end": v(-74, 32.74) * mm});
            skPoint(sketch, "E684.MirrorP", {"position": v(-76.04, 30.31) * mm});
            skPoint(sketch, "E685.MirrorP", {"position": v(-68.02, 31.86) * mm});
            skLineSegment(sketch, "E686.MirrorCS", {"start": v(-80.86, 37.82) * mm, "end": v(-82.44, 35.57) * mm});
            skPoint(sketch, "E687.MirrorP", {"position": v(-88.53, 46.5) * mm});
            skPoint(sketch, "E688.MirrorP", {"position": v(-73.6, 33.2) * mm});
            skLineSegment(sketch, "E689.MirrorCS", {"start": v(-68.62, 31.97) * mm, "end": v(-70.53, 32.3) * mm});
            skPoint(sketch, "E690.MirrorP", {"position": v(-50.8, 35.22) * mm});
            skPoint(sketch, "E691.MirrorP", {"position": v(-55.85, 31.23) * mm});
            skPoint(sketch, "E692.MirrorP", {"position": v(-76.34, 34.78) * mm});
            skPoint(sketch, "E693.MirrorP", {"position": v(-65.45, 31.86) * mm});
            skPoint(sketch, "E694.MirrorP", {"position": v(-71.12, 28.64) * mm});
            skLineSegment(sketch, "E695.MirrorCS", {"start": v(-84.82, 46.78) * mm, "end": v(-85, 48.71) * mm});
            skLineSegment(sketch, "E696.MirrorCS", {"start": v(-64.3, 28.72) * mm, "end": v(-65.24, 31.3) * mm});
            skPoint(sketch, "E697.MirrorP", {"position": v(-48.43, 49.32) * mm});
            skPoint(sketch, "E698.MirrorP", {"position": v(-85.05, 49.32) * mm});
            skPoint(sketch, "E699.MirrorP", {"position": v(-57.14, 34.78) * mm});
            skLineSegment(sketch, "E700.MirrorCS", {"start": v(-85.63, 49.16) * mm, "end": v(-88.28, 48.45) * mm});
            skPoint(sketch, "E701.MirrorP", {"position": v(-80.52, 38.31) * mm});
            skPoint(sketch, "E702.MirrorP", {"position": v(-47.74, 39.52) * mm});
            skPoint(sketch, "E703.MirrorP", {"position": v(-55.18, 36.09) * mm});
            skPoint(sketch, "E704.MirrorP", {"position": v(-48.7, 46.18) * mm});
            skPoint(sketch, "E705.MirrorP", {"position": v(-82.17, 40.77) * mm});
            skPoint(sketch, "E706.MirrorP", {"position": v(-83.72, 43.52) * mm});
            skLineSegment(sketch, "E707.MirrorCS", {"start": v(-78.72, 36.52) * mm, "end": v(-80.09, 37.89) * mm});
            skLineSegment(sketch, "E708.MirrorCS", {"start": v(-62.35, 31.8) * mm, "end": v(-62.35, 29.06) * mm});
            skPoint(sketch, "E709.MirrorP", {"position": v(-64.16, 28.32) * mm});
            skLineSegment(sketch, "E710.MirrorCS", {"start": v(-71.12, 28.64) * mm, "end": v(-69.31, 28.32) * mm, "construction": true});
            skPoint(sketch, "E711.MirrorP", {"position": v(-78.29, 36.09) * mm});
            skPoint(sketch, "E712.MirrorP", {"position": v(-52.96, 38.31) * mm});
            skLineSegment(sketch, "E713.MirrorCS", {"start": v(-64.85, 31.97) * mm, "end": v(-62.95, 32.3) * mm});
            skPoint(sketch, "E714.MirrorP", {"position": v(-51.3, 40.77) * mm});
            skPoint(sketch, "E715.MirrorP", {"position": v(-44.78, 48.34) * mm});
            skPoint(sketch, "E716.MirrorP", {"position": v(-84.77, 46.18) * mm});
            skLineSegment(sketch, "E717.MirrorCS", {"start": v(-85.33, 39.66) * mm, "end": v(-82.74, 40.57) * mm});
            skPoint(sketch, "E718.MirrorP", {"position": v(-59.86, 33.2) * mm});
            skPoint(sketch, "E719.MirrorP", {"position": v(-81.38, 33.92) * mm});
            skLineSegment(sketch, "E720.MirrorCS", {"start": v(-84.18, 43.13) * mm, "end": v(-86.3, 41.4) * mm});
            skLineSegment(sketch, "E721.MirrorCS", {"start": v(-82.47, 41.3) * mm, "end": v(-83.42, 42.99) * mm});
            skPoint(sketch, "E722.MirrorP", {"position": v(-86.63, 41.12) * mm});
            skLineSegment(sketch, "E723.MirrorCS", {"start": v(-88.1, 46.47) * mm, "end": v(-85.38, 46.23) * mm});
            skSolve(sketch);
        }
        {
            var Q0;
            Q0 = qSketchRegion(id + "F1", true);
            extrude(context, id + "F2", {"entities" : qUnion([Q0]), "depth" : 6.35 * mm});
        }
        {
            var Q0;
            Q0=makeQuery(id+"F0.imprint","IMPRINT",FACE,{"disambiguationData":[TD([[makeQuery(id+"F0.imprint","IMPRINT",EDGE,{"derivedFrom":sQuery(id+"F0.wireOp",EDGE,"E1")}),-1.0]])]});
            var Q1;
            Q1=makeQuery(id+"F0.imprint","IMPRINT",FACE,{"disambiguationData":[TD([[makeQuery(id+"F0.imprint","IMPRINT",EDGE,{"derivedFrom":sQuery(id+"F0.wireOp",EDGE,"E98.MirrorCS")}),-1.0]])]});
            var Q2;
            {var subQ1=sQuery(id+"F0.wireOp",EDGE,"E108.MirrorCS");Q2=makeQuery(id+"F0.imprint","IMPRINT",FACE,{"disambiguationData":[TD([[makeQuery(id+"F0.imprint","IMPRINT",EDGE,{"derivedFrom":subQ1}),-1.0]])]});}
            var Q3;
            Q3=makeQuery(id+"F0.imprint","IMPRINT",FACE,{"disambiguationData":[TD([[makeQuery(id+"F0.imprint","IMPRINT",EDGE,{"derivedFrom":sQuery(id+"F0.wireOp",EDGE,"E57")}),1.0]])]});
            var Q4;
            Q4=makeQuery(id+"F0.imprint","IMPRINT",FACE,{"disambiguationData":[TD([[makeQuery(id+"F0.imprint","IMPRINT",EDGE,{"derivedFrom":sQuery(id+"F0.wireOp",EDGE,"E304.MirrorCS")}),1.0]])]});
            var Q5;
            Q5=makeQuery(id+"F0.imprint","IMPRINT",FACE,{"disambiguationData":[TD([[makeQuery(id+"F0.imprint","IMPRINT",EDGE,{"derivedFrom":sQuery(id+"F0.wireOp",EDGE,"E235.MirrorCS")}),1.0]])]});
            var Q6;
            {var subQ6=sQuery(id+"F0.wireOp",EDGE,"E232.MirrorCS");Q6=makeQuery(id+"F0.imprint","IMPRINT",FACE,{"disambiguationData":[TD([[makeQuery(id+"F0.imprint","IMPRINT",EDGE,{"derivedFrom":subQ6}),-1.0]])]});}
            var Q7;
            {var subQ1=sQuery(id+"F0.wireOp",EDGE,"E226.MirrorCS");Q7=makeQuery(id+"F0.imprint","IMPRINT",FACE,{"disambiguationData":[TD([[makeQuery(id+"F0.imprint","IMPRINT",EDGE,{"derivedFrom":subQ1}),1.0]])]});}
            var Q8;
            Q8=makeQuery(id+"F0.imprint","IMPRINT",FACE,{"disambiguationData":[TD([[makeQuery(id+"F0.imprint","IMPRINT",EDGE,{"derivedFrom":sQuery(id+"F0.wireOp",EDGE,"E75")}),1.0]])]});
            var Q9;
            {var subQ4=sQuery(id+"F0.wireOp",EDGE,"E316.MirrorCS");Q9=makeQuery(id+"F0.imprint","IMPRINT",FACE,{"disambiguationData":[TD([[makeQuery(id+"F0.imprint","IMPRINT",EDGE,{"derivedFrom":subQ4}),-1.0]])]});}
            var Q10;
            Q10=makeQuery(id+"F0.imprint","IMPRINT",FACE,{"disambiguationData":[TD([[makeQuery(id+"F0.imprint","IMPRINT",EDGE,{"derivedFrom":sQuery(id+"F0.wireOp",EDGE,"E259.MirrorCS")}),1.0]])]});
            var Q11;
            Q11=makeQuery(id+"F0.imprint","IMPRINT",FACE,{"disambiguationData":[TD([[makeQuery(id+"F0.imprint","IMPRINT",EDGE,{"derivedFrom":sQuery(id+"F0.wireOp",EDGE,"E223.MirrorCS")}),-1.0]])]});
            var Q12;
            {var subQ0=sQuery(id+"F0.wireOp",EDGE,"E14");Q12=makeQuery(id+"F0.imprint","IMPRINT",FACE,{"disambiguationData":[TD([[makeQuery(id+"F0.imprint","IMPRINT",EDGE,{"derivedFrom":subQ0}),1.0]])]});}
            var Q13;
            Q13=makeQuery(id+"F0.imprint","IMPRINT",FACE,{"disambiguationData":[TD([[makeQuery(id+"F0.imprint","IMPRINT",EDGE,{"derivedFrom":sQuery(id+"F0.wireOp",EDGE,"E240.MirrorCS")}),1.0]])]});
            var Q14;
            Q14=makeQuery(id+"F0.imprint","IMPRINT",FACE,{"disambiguationData":[TD([[makeQuery(id+"F0.imprint","IMPRINT",EDGE,{"derivedFrom":sQuery(id+"F0.wireOp",EDGE,"E43")}),-1.0]])]});
            var Q15;
            {var subQ4=sQuery(id+"F0.wireOp",EDGE,"E238.MirrorCS");Q15=makeQuery(id+"F0.imprint","IMPRINT",FACE,{"disambiguationData":[TD([[makeQuery(id+"F0.imprint","IMPRINT",EDGE,{"derivedFrom":subQ4}),1.0]])]});}
            var Q16;
            {var subQ4=sQuery(id+"F0.wireOp",EDGE,"E32");Q16=makeQuery(id+"F0.imprint","IMPRINT",FACE,{"disambiguationData":[TD([[makeQuery(id+"F0.imprint","IMPRINT",EDGE,{"derivedFrom":subQ4}),1.0]])]});}
            var Q17;
            Q17=makeQuery(id+"F0.imprint","IMPRINT",FACE,{"disambiguationData":[TD([[makeQuery(id+"F0.imprint","IMPRINT",EDGE,{"derivedFrom":sQuery(id+"F0.wireOp",EDGE,"E104.MirrorCS")}),1.0]])]});
            var Q18;
            Q18=makeQuery(id+"F0.imprint","IMPRINT",FACE,{"disambiguationData":[TD([[makeQuery(id+"F0.imprint","IMPRINT",EDGE,{"derivedFrom":sQuery(id+"F0.wireOp",EDGE,"E84")}),1.0]])]});
            var Q19;
            {var subQ0=sQuery(id+"F0.wireOp",EDGE,"E111.MirrorCS");Q19=makeQuery(id+"F0.imprint","IMPRINT",FACE,{"disambiguationData":[TD([[makeQuery(id+"F0.imprint","IMPRINT",EDGE,{"derivedFrom":subQ0}),-1.0]])]});}
            var Q20;
            Q20=makeQuery(id+"F0.imprint","IMPRINT",FACE,{"disambiguationData":[TD([[makeQuery(id+"F0.imprint","IMPRINT",EDGE,{"derivedFrom":sQuery(id+"F0.wireOp",EDGE,"E52")}),-1.0]])]});
            var Q21;
            Q21=makeQuery(id+"F0.imprint","IMPRINT",FACE,{"disambiguationData":[TD([[makeQuery(id+"F0.imprint","IMPRINT",EDGE,{"derivedFrom":sQuery(id+"F0.wireOp",EDGE,"E60")}),-1.0]])]});
            var Q22;
            {var subQ1=sQuery(id+"F0.wireOp",EDGE,"E310.MirrorCS");Q22=makeQuery(id+"F0.imprint","IMPRINT",FACE,{"disambiguationData":[TD([[makeQuery(id+"F0.imprint","IMPRINT",EDGE,{"derivedFrom":subQ1}),1.0]])]});}
            var Q23;
            Q23=makeQuery(id+"F0.imprint","IMPRINT",FACE,{"disambiguationData":[TD([[makeQuery(id+"F0.imprint","IMPRINT",EDGE,{"derivedFrom":sQuery(id+"F0.wireOp",EDGE,"E222.MirrorCS")}),1.0]])]});
            var Q24;
            Q24=makeQuery(id+"F0.imprint","IMPRINT",FACE,{"disambiguationData":[TD([[makeQuery(id+"F0.imprint","IMPRINT",EDGE,{"derivedFrom":sQuery(id+"F0.wireOp",EDGE,"E95.MirrorCS")}),1.0]])]});
            var Q25;
            Q25=makeQuery(id+"F0.imprint","IMPRINT",FACE,{"disambiguationData":[TD([[makeQuery(id+"F0.imprint","IMPRINT",EDGE,{"derivedFrom":sQuery(id+"F0.wireOp",EDGE,"E254.MirrorCS")}),-1.0]])]});
            var Q26;
            Q26=makeQuery(id+"F0.imprint","IMPRINT",FACE,{"disambiguationData":[TD([[makeQuery(id+"F0.imprint","IMPRINT",EDGE,{"derivedFrom":sQuery(id+"F0.wireOp",EDGE,"E242.MirrorCS")}),1.0]])]});
            var Q27;
            Q27=makeQuery(id+"F0.imprint","IMPRINT",FACE,{"disambiguationData":[TD([[makeQuery(id+"F0.imprint","IMPRINT",EDGE,{"derivedFrom":sQuery(id+"F0.wireOp",EDGE,"E25")}),-1.0]])]});
            var Q28;
            {var subQ6=sQuery(id+"F0.wireOp",EDGE,"E273.MirrorCS");Q28=makeQuery(id+"F0.imprint","IMPRINT",FACE,{"disambiguationData":[TD([[makeQuery(id+"F0.imprint","IMPRINT",EDGE,{"derivedFrom":subQ6}),-1.0]])]});}
            var Q29;
            Q29=makeQuery(id+"F0.imprint","IMPRINT",FACE,{"disambiguationData":[TD([[makeQuery(id+"F0.imprint","IMPRINT",EDGE,{"derivedFrom":sQuery(id+"F0.wireOp",EDGE,"E87")}),-1.0]])]});
            var Q30;
            Q30=makeQuery(id+"F0.imprint","IMPRINT",FACE,{"disambiguationData":[TD([[makeQuery(id+"F0.imprint","IMPRINT",EDGE,{"derivedFrom":sQuery(id+"F0.wireOp",EDGE,"E78")}),-1.0]])]});
            var Q31;
            Q31=makeQuery(id+"F0.imprint","IMPRINT",FACE,{"disambiguationData":[TD([[makeQuery(id+"F0.imprint","IMPRINT",EDGE,{"derivedFrom":sQuery(id+"F0.wireOp",EDGE,"E347.MirrorCS")}),1.0]])]});
            var Q32;
            Q32=makeQuery(id+"F0.imprint","IMPRINT",FACE,{"disambiguationData":[TD([[makeQuery(id+"F0.imprint","IMPRINT",EDGE,{"derivedFrom":sQuery(id+"F0.wireOp",EDGE,"E294.MirrorCS")}),-1.0]])]});
            var Q33;
            {var subQ1=sQuery(id+"F0.wireOp",EDGE,"E247.MirrorCS");Q33=makeQuery(id+"F0.imprint","IMPRINT",FACE,{"disambiguationData":[TD([[makeQuery(id+"F0.imprint","IMPRINT",EDGE,{"derivedFrom":subQ1}),1.0]])]});}
            var Q34;
            {var subQ1=sQuery(id+"F0.wireOp",EDGE,"E234.MirrorCS");Q34=makeQuery(id+"F0.imprint","IMPRINT",FACE,{"disambiguationData":[TD([[makeQuery(id+"F0.imprint","IMPRINT",EDGE,{"derivedFrom":subQ1}),1.0]])]});}
            var Q35;
            {var subQ0=sQuery(id+"F0.wireOp",EDGE,"E274.MirrorCS");Q35=makeQuery(id+"F0.imprint","IMPRINT",FACE,{"disambiguationData":[TD([[makeQuery(id+"F0.imprint","IMPRINT",EDGE,{"derivedFrom":subQ0}),-1.0]])]});}
            var Q36;
            Q36=makeQuery(id+"F0.imprint","IMPRINT",FACE,{"disambiguationData":[TD([[makeQuery(id+"F0.imprint","IMPRINT",EDGE,{"derivedFrom":sQuery(id+"F0.wireOp",EDGE,"E22")}),1.0]])]});
            var Q37;
            {var subQ0=sQuery(id+"F0.wireOp",EDGE,"E339.MirrorCS");Q37=makeQuery(id+"F0.imprint","IMPRINT",FACE,{"disambiguationData":[TD([[makeQuery(id+"F0.imprint","IMPRINT",EDGE,{"derivedFrom":subQ0}),1.0]])]});}
            var Q38;
            Q38=makeQuery(id+"F0.imprint","IMPRINT",FACE,{"disambiguationData":[TD([[makeQuery(id+"F0.imprint","IMPRINT",EDGE,{"derivedFrom":sQuery(id+"F0.wireOp",EDGE,"E40")}),1.0]])]});
            var Q39;
            {var subQ5=sQuery(id+"F0.wireOp",EDGE,"E237.MirrorCS");Q39=makeQuery(id+"F0.imprint","IMPRINT",FACE,{"disambiguationData":[TD([[makeQuery(id+"F0.imprint","IMPRINT",EDGE,{"derivedFrom":subQ5}),1.0]])]});}
            var Q40;
            Q40=makeQuery(id+"F0.imprint","IMPRINT",FACE,{"disambiguationData":[TD([[makeQuery(id+"F0.imprint","IMPRINT",EDGE,{"derivedFrom":sQuery(id+"F0.wireOp",EDGE,"E66")}),1.0]])]});
            var Q41;
            Q41=makeQuery(id+"F0.imprint","IMPRINT",FACE,{"disambiguationData":[TD([[makeQuery(id+"F0.imprint","IMPRINT",EDGE,{"derivedFrom":sQuery(id+"F0.wireOp",EDGE,"E272.MirrorCS")}),-1.0]])]});
            var Q42;
            {var subQ4=sQuery(id+"F0.wireOp",EDGE,"E229.MirrorCS");Q42=makeQuery(id+"F0.imprint","IMPRINT",FACE,{"disambiguationData":[TD([[makeQuery(id+"F0.imprint","IMPRINT",EDGE,{"derivedFrom":subQ4}),-1.0]])]});}
            var Q43;
            {var subQ1=sQuery(id+"F0.wireOp",EDGE,"E31");Q43=makeQuery(id+"F0.imprint","IMPRINT",FACE,{"disambiguationData":[TD([[makeQuery(id+"F0.imprint","IMPRINT",EDGE,{"derivedFrom":subQ1}),1.0]])]});}
            var Q44;
            {var subQ1=sQuery(id+"F0.wireOp",EDGE,"E307.MirrorCS");Q44=makeQuery(id+"F0.imprint","IMPRINT",FACE,{"disambiguationData":[TD([[makeQuery(id+"F0.imprint","IMPRINT",EDGE,{"derivedFrom":subQ1}),-1.0]])]});}
            var Q45;
            Q45=makeQuery(id+"F0.imprint","IMPRINT",FACE,{"disambiguationData":[TD([[makeQuery(id+"F0.imprint","IMPRINT",EDGE,{"derivedFrom":sQuery(id+"F0.wireOp",EDGE,"E96.MirrorCS")}),1.0]])]});
            var Q46;
            Q46=makeQuery(id+"F0.imprint","IMPRINT",FACE,{"disambiguationData":[TD([[makeQuery(id+"F0.imprint","IMPRINT",EDGE,{"derivedFrom":sQuery(id+"F0.wireOp",EDGE,"E4")}),1.0]])]});
            var Q47;
            Q47=makeQuery(id+"F0.imprint","IMPRINT",FACE,{"disambiguationData":[TD([[makeQuery(id+"F0.imprint","IMPRINT",EDGE,{"derivedFrom":sQuery(id+"F0.wireOp",EDGE,"E249.MirrorCS")}),1.0]])]});
            var Q48;
            Q48=makeQuery(id+"F0.imprint","IMPRINT",FACE,{"disambiguationData":[TD([[makeQuery(id+"F0.imprint","IMPRINT",EDGE,{"derivedFrom":sQuery(id+"F0.wireOp",EDGE,"E121.MirrorCS")}),-1.0]])]});
            var Q49;
            {var subQ4=sQuery(id+"F0.wireOp",EDGE,"E300.MirrorCS");Q49=makeQuery(id+"F0.imprint","IMPRINT",FACE,{"disambiguationData":[TD([[makeQuery(id+"F0.imprint","IMPRINT",EDGE,{"derivedFrom":subQ4}),-1.0]])]});}
            var Q50;
            {var subQ4=sQuery(id+"F0.wireOp",EDGE,"E244.MirrorCS");Q50=makeQuery(id+"F0.imprint","IMPRINT",FACE,{"disambiguationData":[TD([[makeQuery(id+"F0.imprint","IMPRINT",EDGE,{"derivedFrom":subQ4}),1.0]])]});}
            var Q51;
            Q51=makeQuery(id+"F0.imprint","IMPRINT",FACE,{"disambiguationData":[TD([[makeQuery(id+"F0.imprint","IMPRINT",EDGE,{"derivedFrom":sQuery(id+"F0.wireOp",EDGE,"E225.MirrorCS")}),1.0]])]});
            var Q52;
            Q52=makeQuery(id+"F0.imprint","IMPRINT",FACE,{"disambiguationData":[TD([[makeQuery(id+"F0.imprint","IMPRINT",EDGE,{"derivedFrom":sQuery(id+"F0.wireOp",EDGE,"E103.MirrorCS")}),1.0]])]});
            var Q53;
            Q53=makeQuery(id+"F0.imprint","IMPRINT",FACE,{"disambiguationData":[TD([[makeQuery(id+"F0.imprint","IMPRINT",EDGE,{"derivedFrom":sQuery(id+"F0.wireOp",EDGE,"E233.MirrorCS")}),1.0]])]});
            var Q54;
            {var subQ1=sQuery(id+"F0.wireOp",EDGE,"E305.MirrorCS");Q54=makeQuery(id+"F0.imprint","IMPRINT",FACE,{"disambiguationData":[TD([[makeQuery(id+"F0.imprint","IMPRINT",EDGE,{"derivedFrom":subQ1}),1.0]])]});}
            var Q55;
            Q55=makeQuery(id+"F0.imprint","IMPRINT",FACE,{"disambiguationData":[TD([[makeQuery(id+"F0.imprint","IMPRINT",EDGE,{"derivedFrom":sQuery(id+"F0.wireOp",EDGE,"E94.MirrorCS")}),1.0]])]});
            var Q56;
            {var subQ5=sQuery(id+"F0.wireOp",EDGE,"E115.MirrorCS");Q56=makeQuery(id+"F0.imprint","IMPRINT",FACE,{"disambiguationData":[TD([[makeQuery(id+"F0.imprint","IMPRINT",EDGE,{"derivedFrom":subQ5}),-1.0]])]});}
            var Q57;
            Q57=makeQuery(id+"F0.imprint","IMPRINT",FACE,{"disambiguationData":[TD([[makeQuery(id+"F0.imprint","IMPRINT",EDGE,{"derivedFrom":sQuery(id+"F0.wireOp",EDGE,"E231.MirrorCS")}),-1.0]])]});
            var Q58;
            {var subQ4=sQuery(id+"F0.wireOp",EDGE,"E97.MirrorCS");Q58=makeQuery(id+"F0.imprint","IMPRINT",FACE,{"disambiguationData":[TD([[makeQuery(id+"F0.imprint","IMPRINT",EDGE,{"derivedFrom":subQ4}),-1.0]])]});}
            var Q59;
            Q59=makeQuery(id+"F0.imprint","IMPRINT",FACE,{"disambiguationData":[TD([[makeQuery(id+"F0.imprint","IMPRINT",EDGE,{"derivedFrom":sQuery(id+"F0.wireOp",EDGE,"E109.MirrorCS")}),-1.0]])]});
            var Q60;
            Q60=makeQuery(id+"F0.imprint","IMPRINT",FACE,{"disambiguationData":[TD([[makeQuery(id+"F0.imprint","IMPRINT",EDGE,{"derivedFrom":sQuery(id+"F0.wireOp",EDGE,"E132.MirrorCS")}),-1.0]])]});
            var Q61;
            Q61=makeQuery(id+"F0.imprint","IMPRINT",FACE,{"disambiguationData":[TD([[makeQuery(id+"F0.imprint","IMPRINT",EDGE,{"derivedFrom":sQuery(id+"F0.wireOp",EDGE,"E139.MirrorCS")}),-1.0]])]});
            var Q62;
            {var subQ1=sQuery(id+"F0.wireOp",EDGE,"E248.MirrorCS");Q62=makeQuery(id+"F0.imprint","IMPRINT",FACE,{"disambiguationData":[TD([[makeQuery(id+"F0.imprint","IMPRINT",EDGE,{"derivedFrom":subQ1}),-1.0]])]});}
            var Q63;
            Q63=makeQuery(id+"F0.imprint","IMPRINT",FACE,{"disambiguationData":[TD([[makeQuery(id+"F0.imprint","IMPRINT",EDGE,{"derivedFrom":sQuery(id+"F0.wireOp",EDGE,"E337.MirrorCS")}),1.0]])]});
            var Q64;
            {var subQ4=sQuery(id+"F0.wireOp",EDGE,"E137.MirrorCS");Q64=makeQuery(id+"F0.imprint","IMPRINT",FACE,{"disambiguationData":[TD([[makeQuery(id+"F0.imprint","IMPRINT",EDGE,{"derivedFrom":subQ4}),-1.0]])]});}
            var Q65;
            {var subQ5=sQuery(id+"F0.wireOp",EDGE,"E295.MirrorCS");Q65=makeQuery(id+"F0.imprint","IMPRINT",FACE,{"disambiguationData":[TD([[makeQuery(id+"F0.imprint","IMPRINT",EDGE,{"derivedFrom":subQ5}),1.0]])]});}
            var Q66;
            Q66=makeQuery(id+"F0.imprint","IMPRINT",FACE,{"disambiguationData":[TD([[makeQuery(id+"F0.imprint","IMPRINT",EDGE,{"derivedFrom":sQuery(id+"F0.wireOp",EDGE,"E264.MirrorCS")}),-1.0]])]});
            var Q67;
            {var subQ4=sQuery(id+"F0.wireOp",EDGE,"E124.MirrorCS");Q67=makeQuery(id+"F0.imprint","IMPRINT",FACE,{"disambiguationData":[TD([[makeQuery(id+"F0.imprint","IMPRINT",EDGE,{"derivedFrom":subQ4}),-1.0]])]});}
            var Q68;
            Q68=makeQuery(id+"F0.imprint","IMPRINT",FACE,{"disambiguationData":[TD([[makeQuery(id+"F0.imprint","IMPRINT",EDGE,{"derivedFrom":sQuery(id+"F0.wireOp",EDGE,"E279.MirrorCS")}),1.0]])]});
            var Q69;
            Q69=makeQuery(id+"F0.imprint","IMPRINT",FACE,{"disambiguationData":[TD([[makeQuery(id+"F0.imprint","IMPRINT",EDGE,{"derivedFrom":sQuery(id+"F0.wireOp",EDGE,"E7")}),-1.0]])]});
            var Q70;
            Q70=makeQuery(id+"F0.imprint","IMPRINT",FACE,{"disambiguationData":[TD([[makeQuery(id+"F0.imprint","IMPRINT",EDGE,{"derivedFrom":sQuery(id+"F0.wireOp",EDGE,"E93.MirrorCS")}),1.0]])]});
            var Q71;
            {var subQ4=sQuery(id+"F0.wireOp",EDGE,"E12");Q71=makeQuery(id+"F0.imprint","IMPRINT",FACE,{"disambiguationData":[TD([[makeQuery(id+"F0.imprint","IMPRINT",EDGE,{"derivedFrom":subQ4}),1.0]])]});}
            var Q72;
            Q72=makeQuery(id+"F0.imprint","IMPRINT",FACE,{"disambiguationData":[TD([[makeQuery(id+"F0.imprint","IMPRINT",EDGE,{"derivedFrom":sQuery(id+"F0.wireOp",EDGE,"E69")}),-1.0]])]});
            var Q73;
            {var subQ0=sQuery(id+"F0.wireOp",EDGE,"E110.MirrorCS");Q73=makeQuery(id+"F0.imprint","IMPRINT",FACE,{"disambiguationData":[TD([[makeQuery(id+"F0.imprint","IMPRINT",EDGE,{"derivedFrom":subQ0}),-1.0]])]});}
            var Q74;
            {var subQ1=sQuery(id+"F0.wireOp",EDGE,"E134.MirrorCS");Q74=makeQuery(id+"F0.imprint","IMPRINT",FACE,{"disambiguationData":[TD([[makeQuery(id+"F0.imprint","IMPRINT",EDGE,{"derivedFrom":subQ1}),-1.0]])]});}
            var Q75;
            {var subQ0=sQuery(id+"F0.wireOp",EDGE,"E255.MirrorCS");Q75=makeQuery(id+"F0.imprint","IMPRINT",FACE,{"disambiguationData":[TD([[makeQuery(id+"F0.imprint","IMPRINT",EDGE,{"derivedFrom":subQ0}),-1.0]])]});}
            var Q76;
            {var subQ2=sQuery(id+"F0.wireOp",EDGE,"E100.MirrorCS");Q76=makeQuery(id+"F0.imprint","IMPRINT",FACE,{"disambiguationData":[TD([[makeQuery(id+"F0.imprint","IMPRINT",EDGE,{"derivedFrom":subQ2}),-1.0]])]});}
            var Q77;
            Q77=makeQuery(id+"F0.imprint","IMPRINT",FACE,{"disambiguationData":[TD([[makeQuery(id+"F0.imprint","IMPRINT",EDGE,{"derivedFrom":sQuery(id+"F0.wireOp",EDGE,"E49")}),1.0]])]});
            var Q78;
            {var subQ4=sQuery(id+"F0.wireOp",EDGE,"E275.MirrorCS");Q78=makeQuery(id+"F0.imprint","IMPRINT",FACE,{"disambiguationData":[TD([[makeQuery(id+"F0.imprint","IMPRINT",EDGE,{"derivedFrom":subQ4}),1.0]])]});}
            var Q79;
            {var subQ5=sQuery(id+"F0.wireOp",EDGE,"E303.MirrorCS");Q79=makeQuery(id+"F0.imprint","IMPRINT",FACE,{"disambiguationData":[TD([[makeQuery(id+"F0.imprint","IMPRINT",EDGE,{"derivedFrom":subQ5}),1.0]])]});}
            var Q80;
            {var subQ1=sQuery(id+"F0.wireOp",EDGE,"E332.MirrorCS");Q80=makeQuery(id+"F0.imprint","IMPRINT",FACE,{"disambiguationData":[TD([[makeQuery(id+"F0.imprint","IMPRINT",EDGE,{"derivedFrom":subQ1}),-1.0]])]});}
            extrude(context, id + "F3", {"entities" : qUnion([Q0, Q1, Q2, Q3, Q4, Q5, Q6, Q7, Q8, Q9, Q10, Q11, Q12, Q13, Q14, Q15, Q16, Q17, Q18, Q19, Q20, Q21, Q22, Q23, Q24, Q25, Q26, Q27, Q28, Q29, Q30, Q31, Q32, Q33, Q34, Q35, Q36, Q37, Q38, Q39, Q40, Q41, Q42, Q43, Q44, Q45, Q46, Q47, Q48, Q49, Q50, Q51, Q52, Q53, Q54, Q55, Q56, Q57, Q58, Q59, Q60, Q61, Q62, Q63, Q64, Q65, Q66, Q67, Q68, Q69, Q70, Q71, Q72, Q73, Q74, Q75, Q76, Q77, Q78, Q79, Q80]), "depth" : 12.7 * mm});
        }
    });
